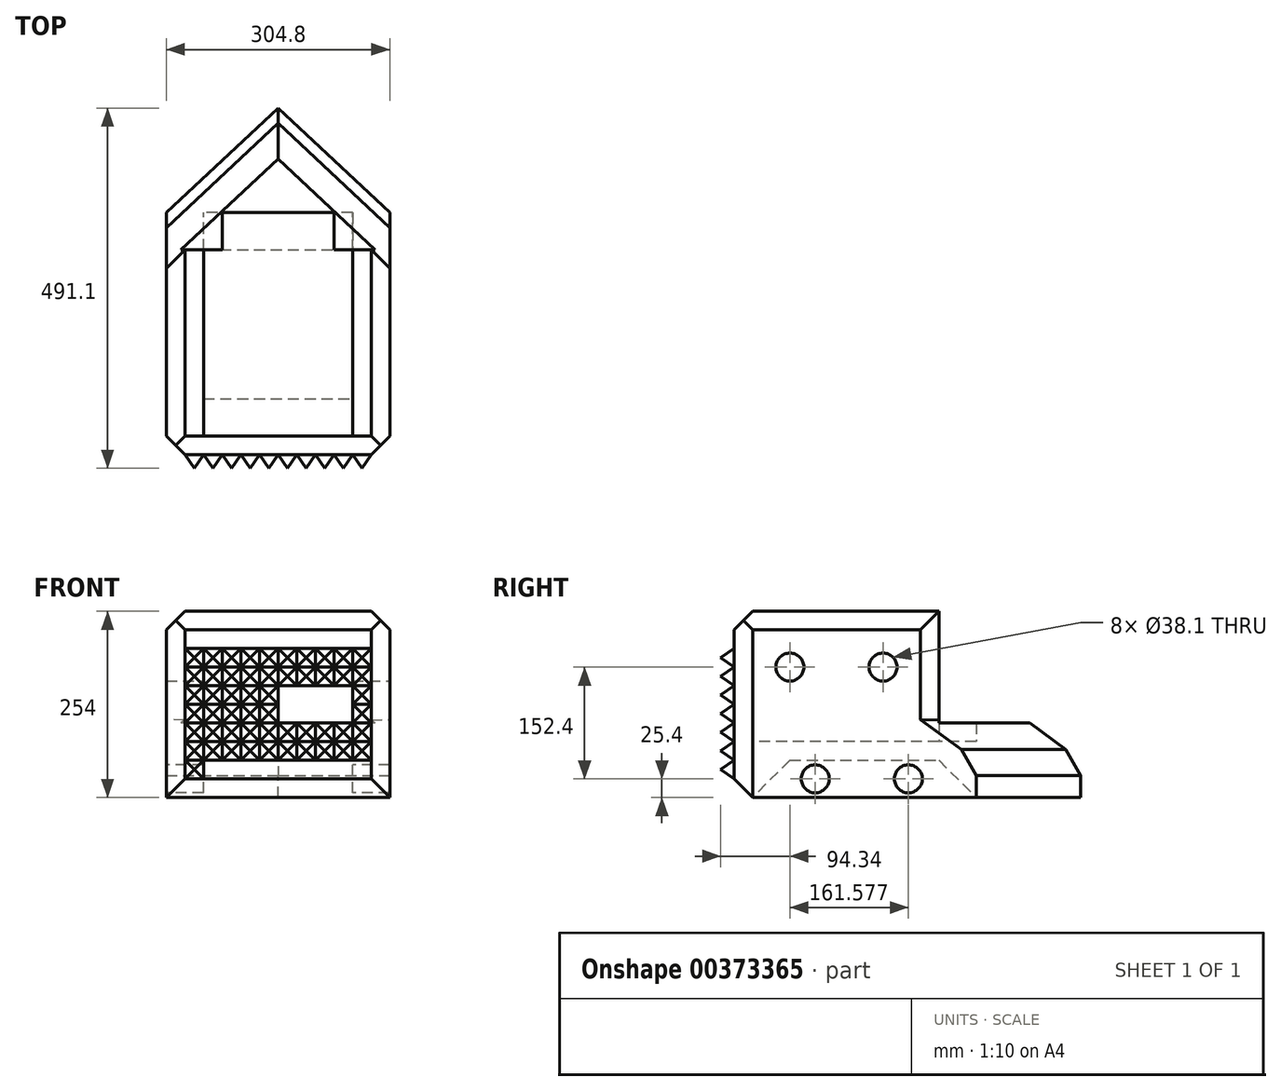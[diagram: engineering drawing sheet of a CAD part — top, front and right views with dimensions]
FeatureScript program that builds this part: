
annotation { "Feature Type Name" : "Feature", "Feature Type Description" : "" }
export const myFeature = defineFeature(function(context is Context, id is Id, definition is map)
    precondition{}
    {
        {
            var Q0;
            Q0=qCreatedBy(makeId("Top.planeOp"),FACE);
            var sketch = newSketch(context, id + "F0", { "sketchPlane" : qUnion([Q0])});
            skLineSegment(sketch, "E0.bottom", {"start": v(-152.4, 152.4) * mm, "end": v(152.4, 152.4) * mm});
            skLineSegment(sketch, "E0.top", {"start": v(-152.4, -152.4) * mm, "end": v(152.4, -152.4) * mm});
            skLineSegment(sketch, "E0.left", {"start": v(-152.4, 152.4) * mm, "end": v(-152.4, -152.4) * mm});
            skLineSegment(sketch, "E0.right", {"start": v(152.4, 152.4) * mm, "end": v(152.4, -152.4) * mm});
            skPoint(sketch, "E0.middle", {"position": v(0, 0) * mm});
            skSolve(sketch);
        }
        {
            var Q0;
            Q0 = qSketchRegion(id + "F0", true);
            extrude(context, id + "F1", {"entities" : qUnion([Q0]), "depth" : 25.4 * mm});
        }
        {
            var Q0;
            Q0=makeQuery(id+"F1.opExtrude","CAP_FACE",FACE,{"disambiguationData":[OSD([sQuery(id+"F0.wireOp",EDGE,"E0.bottom"),sQuery(id+"F0.wireOp",EDGE,"E0.top"),sQuery(id+"F0.wireOp",EDGE,"E0.left"),sQuery(id+"F0.wireOp",EDGE,"E0.right")])],"isStart":false});
            var sketch = newSketch(context, id + "F2", { "sketchPlane" : qUnion([Q0])});
            skLineSegment(sketch, "E1.bottom", {"start": v(-152.4, 152.4) * mm, "end": v(-101.6, 152.4) * mm});
            skLineSegment(sketch, "E1.top", {"start": v(-152.4, -152.4) * mm, "end": v(-101.6, -152.4) * mm});
            skLineSegment(sketch, "E1.left", {"start": v(-152.4, 152.4) * mm, "end": v(-152.4, -152.4) * mm});
            skLineSegment(sketch, "E1.right", {"start": v(-101.6, 152.4) * mm, "end": v(-101.6, -152.4) * mm});
            skLineSegment(sketch, "E2.bottom", {"start": v(152.4, -152.4) * mm, "end": v(101.6, -152.4) * mm});
            skLineSegment(sketch, "E2.top", {"start": v(152.4, 152.4) * mm, "end": v(101.6, 152.4) * mm});
            skLineSegment(sketch, "E2.left", {"start": v(152.4, -152.4) * mm, "end": v(152.4, 152.4) * mm});
            skLineSegment(sketch, "E2.right", {"start": v(101.6, -152.4) * mm, "end": v(101.6, 152.4) * mm});
            skLineSegment(sketch, "E3.bottom", {"start": v(-101.6, 152.4) * mm, "end": v(-76.2, 152.4) * mm});
            skLineSegment(sketch, "E3.top", {"start": v(-101.6, 101.6) * mm, "end": v(-76.2, 101.6) * mm});
            skLineSegment(sketch, "E3.left", {"start": v(-101.6, 152.4) * mm, "end": v(-101.6, 101.6) * mm});
            skLineSegment(sketch, "E3.right", {"start": v(-76.2, 152.4) * mm, "end": v(-76.2, 101.6) * mm});
            skLineSegment(sketch, "E4.bottom", {"start": v(101.6, 152.4) * mm, "end": v(76.2, 152.4) * mm});
            skLineSegment(sketch, "E4.top", {"start": v(101.6, 101.6) * mm, "end": v(76.2, 101.6) * mm});
            skLineSegment(sketch, "E4.left", {"start": v(101.6, 152.4) * mm, "end": v(101.6, 101.6) * mm});
            skLineSegment(sketch, "E4.right", {"start": v(76.2, 152.4) * mm, "end": v(76.2, 101.6) * mm});
            skSolve(sketch);
        }
        {
            var Q0;
            Q0=makeQuery(id+"F2.imprint","IMPRINT",FACE,{"disambiguationData":[TD([[makeQuery(id+"F2.imprint","IMPRINT",EDGE,{"derivedFrom":sQuery(id+"F2.wireOp",EDGE,"E2.bottom")}),1.0]])]});
            var Q1;
            Q1=makeQuery(id+"F2.imprint","IMPRINT",FACE,{"disambiguationData":[TD([[makeQuery(id+"F2.imprint","IMPRINT",EDGE,{"derivedFrom":sQuery(id+"F2.wireOp",EDGE,"E4.bottom")}),-1.0]])]});
            var Q2;
            Q2=makeQuery(id+"F2.imprint","IMPRINT",FACE,{"disambiguationData":[TD([[makeQuery(id+"F2.imprint","IMPRINT",EDGE,{"derivedFrom":sQuery(id+"F2.wireOp",EDGE,"E3.bottom")}),-1.0]])]});
            var Q3;
            Q3=makeQuery(id+"F2.imprint","IMPRINT",FACE,{"disambiguationData":[TD([[makeQuery(id+"F2.imprint","IMPRINT",EDGE,{"derivedFrom":sQuery(id+"F2.wireOp",EDGE,"E1.bottom")}),-1.0]])]});
            extrude(context, id + "F3", {"entities" : qUnion([Q0, Q1, Q2, Q3]), "operationType" : NewBodyOperationType.ADD, "depth" : 25.4 * mm});
        }
        {
            var Q0;
            Q0=makeQuery(id+"FkGgvWkWBMemayw_1.boolean.opBoolean","MERGE",FACE,{"derivedFrom":[makeQuery(id+"FRFY5aiqNvbobkp_1.boolean.opBoolean","MERGE",FACE,{"derivedFrom":[makeQuery(id+"F3.opExtrude","CAP_FACE",FACE,{"disambiguationData":[OSD([sQuery(id+"F2.wireOp",EDGE,"E1.bottom"),sQuery(id+"F2.wireOp",EDGE,"E1.top"),sQuery(id+"F2.wireOp",EDGE,"E1.left"),sQuery(id+"F2.wireOp",EDGE,"E1.right"),sQuery(id+"F2.wireOp",EDGE,"E2.bottom"),sQuery(id+"F2.wireOp",EDGE,"E2.top"),sQuery(id+"F2.wireOp",EDGE,"E2.left"),sQuery(id+"F2.wireOp",EDGE,"E2.right"),sQuery(id+"F2.wireOp",EDGE,"gtZrgzOz-b58x-KVUL-jsQg-DSi5dSDXwSVX.bottom"),sQuery(id+"F2.wireOp",EDGE,"gtZrgzOz-b58x-KVUL-jsQg-DSi5dSDXwSVX.top"),sQuery(id+"F2.wireOp",EDGE,"E3.bottom"),sQuery(id+"F2.wireOp",EDGE,"E3.top"),sQuery(id+"F2.wireOp",EDGE,"E3.right"),sQuery(id+"F2.wireOp",EDGE,"E4.bottom"),sQuery(id+"F2.wireOp",EDGE,"E4.top"),sQuery(id+"F2.wireOp",EDGE,"E4.right")])],"isStart":false}),makeQuery(id+"FRFY5aiqNvbobkp_1.opExtrude","CAP_FACE",FACE,{"disambiguationData":[OSD([sQuery(id+"FdvoQodGxraJRl4_1.wireOp",EDGE,"ubKTltfd-fttm-ud9w-CVmu-kFfNegf7EsK9"),sQuery(id+"FdvoQodGxraJRl4_1.wireOp",EDGE,"GuVsw8sI-SjNi-WbUd-Ecwz-Xx77keOuN9XW"),sQuery(id+"FdvoQodGxraJRl4_1.wireOp",EDGE,"aaOYgBz2-yths-JL3X-ABsj-uYR8tw8wiFr5")])],"isStart":true})]}),makeQuery(id+"FkGgvWkWBMemayw_1.opExtrude","CAP_FACE",FACE,{"disambiguationData":[OSD([sQuery(id+"FwGnvekFHA1S1A1_1.wireOp",EDGE,"zjP9bahP-IcYc-KR9K-D0dO-XseXDK0v0Trk"),sQuery(id+"FwGnvekFHA1S1A1_1.wireOp",EDGE,"3lqd1lpt-OsAJ-ImGJ-6Shh-clCQJiHXbUOp"),sQuery(id+"FwGnvekFHA1S1A1_1.wireOp",EDGE,"36x9WmHc-cpKm-z8fz-d8IO-fmrlZK17Axvm")])],"isStart":true})]});
            var sketch = newSketch(context, id + "F4", { "sketchPlane" : qUnion([Q0])});
            skLineSegment(sketch, "E5.bottom", {"start": v(-101.6, 101.6) * mm, "end": v(-152.4, 101.6) * mm});
            skLineSegment(sketch, "E5.top", {"start": v(-101.6, -152.4) * mm, "end": v(-152.4, -152.4) * mm});
            skLineSegment(sketch, "E5.left", {"start": v(-101.6, 101.6) * mm, "end": v(-101.6, -152.4) * mm});
            skLineSegment(sketch, "E5.right", {"start": v(-152.4, 101.6) * mm, "end": v(-152.4, -152.4) * mm});
            skLineSegment(sketch, "E6.bottom", {"start": v(152.4, -152.4) * mm, "end": v(101.6, -152.4) * mm});
            skLineSegment(sketch, "E6.top", {"start": v(152.4, 101.6) * mm, "end": v(101.6, 101.6) * mm});
            skLineSegment(sketch, "E6.left", {"start": v(152.4, -152.4) * mm, "end": v(152.4, 101.6) * mm});
            skLineSegment(sketch, "E6.right", {"start": v(101.6, -152.4) * mm, "end": v(101.6, 101.6) * mm});
            skSolve(sketch);
        }
        {
            var Q0;
            Q0 = qSketchRegion(id + "F4", true);
            extrude(context, id + "F5", {"entities" : qUnion([Q0]), "operationType" : NewBodyOperationType.ADD, "depth" : 152.4 * mm});
        }
        {
            var Q0;
            Q0=makeQuery(id+"F1.opExtrude","CAP_FACE",FACE,{"disambiguationData":[OSD([sQuery(id+"F0.wireOp",EDGE,"E0.bottom"),sQuery(id+"F0.wireOp",EDGE,"E0.top"),sQuery(id+"F0.wireOp",EDGE,"E0.left"),sQuery(id+"F0.wireOp",EDGE,"E0.right")])],"isStart":true});
            var sketch = newSketch(context, id + "F6", { "sketchPlane" : qUnion([Q0])});
            skLineSegment(sketch, "E7", {"start": v(152.4, -152.4) * mm, "end": v(0, -295.16) * mm});
            skLineSegment(sketch, "E8", {"start": v(0, -295.16) * mm, "end": v(-152.4, -152.4) * mm});
            skSolve(sketch);
        }
        {
            var Q0;
            Q0=makeQuery(id+"F6.imprint","IMPRINT",FACE,{"disambiguationData":[TD([[makeQuery(id+"F6.imprint","IMPRINT",EDGE,{"derivedFrom":sQuery(id+"F6.wireOp",EDGE,"E7")}),-1.0]])]});
            extrude(context, id + "F7", {"entities" : qUnion([Q0]), "operationType" : NewBodyOperationType.ADD, "oppositeDirection" : true, "depth" : 50.8 * mm});
        }
        {
            var Q0;
            Q0=makeQuery(id+"F7.opExtrude","CAP_EDGE",EDGE,{"disambiguationData":[OSD([sQuery(id+"F6.wireOp",EDGE,"E8")])],"isStart":false});
            var Q1;
            Q1=makeQuery(id+"F7.opExtrude","CAP_EDGE",EDGE,{"disambiguationData":[OSD([sQuery(id+"F6.wireOp",EDGE,"E7")])],"isStart":false});
            chamfer(context, id + "F8", {"entities" : qUnion([Q0, Q1]), "width" : 50.8 * mm, "tangentPropagation" : true});
        }
        {
            var Q0;
            Q0=makeQuery(id+"F5.boolean.opBoolean","MERGE",FACE,{"derivedFrom":[makeQuery(id+"F3.boolean.opBoolean","MERGE",FACE,{"derivedFrom":[makeQuery(id+"F1.opExtrude","SWEPT_FACE",FACE,{"disambiguationData":[OSD([sQuery(id+"F0.wireOp",EDGE,"E0.top")])]}),makeQuery(id+"F3.opExtrude","SWEPT_FACE",FACE,{"disambiguationData":[OSD([sQuery(id+"F2.wireOp",EDGE,"E1.top")])]}),makeQuery(id+"F3.opExtrude","SWEPT_FACE",FACE,{"disambiguationData":[OSD([sQuery(id+"F2.wireOp",EDGE,"E2.bottom")])]})]}),makeQuery(id+"F5.opExtrude","SWEPT_FACE",FACE,{"disambiguationData":[OSD([sQuery(id+"F4.wireOp",EDGE,"8l8OuRup-84i1-PPMk-ahTQ-howiFgtnHGYQ.top")])]}),makeQuery(id+"F5.opExtrude","SWEPT_FACE",FACE,{"disambiguationData":[OSD([sQuery(id+"F4.wireOp",EDGE,"KN1si1wC-PfOw-yzif-CKwp-hQymulGBh6hX.top")])]})]});
            var sketch = newSketch(context, id + "F9", { "sketchPlane" : qUnion([Q0])});
            skLineSegment(sketch, "E9.bottom", {"start": v(-152.4, 203.2) * mm, "end": v(152.4, 203.2) * mm});
            skLineSegment(sketch, "E9.top", {"start": v(-152.4, 0) * mm, "end": v(152.4, 0) * mm});
            skLineSegment(sketch, "E9.left", {"start": v(-152.4, 203.2) * mm, "end": v(-152.4, 0) * mm});
            skLineSegment(sketch, "E9.right", {"start": v(152.4, 203.2) * mm, "end": v(152.4, 0) * mm});
            skSolve(sketch);
        }
        {
            var Q0;
            Q0 = qSketchRegion(id + "F9", true);
            extrude(context, id + "F10", {"entities" : qUnion([Q0]), "operationType" : NewBodyOperationType.ADD, "depth" : 25.4 * mm});
        }
        {
            var Q0;
            Q0=makeQuery(id+"F10.opExtrude","CAP_FACE",FACE,{"disambiguationData":[OSD([sQuery(id+"F9.wireOp",EDGE,"E9.bottom"),sQuery(id+"F9.wireOp",EDGE,"E9.top"),sQuery(id+"F9.wireOp",EDGE,"E9.left"),sQuery(id+"F9.wireOp",EDGE,"E9.right")])],"isStart":false});
            var sketch = newSketch(context, id + "F11", { "sketchPlane" : qUnion([Q0])});
            skLineSegment(sketch, "E10", {"start": v(-152.4, 177.8) * mm, "end": v(152.4, 177.8) * mm});
            skLineSegment(sketch, "E11", {"start": v(-127, 177.8) * mm, "end": v(-127, 25.4) * mm});
            skLineSegment(sketch, "E12", {"start": v(127, 177.8) * mm, "end": v(127, 25.4) * mm});
            skLineSegment(sketch, "E13.bottom", {"start": v(-127, 177.8) * mm, "end": v(-101.6, 177.8) * mm});
            skLineSegment(sketch, "E13.top", {"start": v(-127, 152.4) * mm, "end": v(-101.6, 152.4) * mm});
            skLineSegment(sketch, "E13.left", {"start": v(-127, 177.8) * mm, "end": v(-127, 152.4) * mm});
            skLineSegment(sketch, "E13.right", {"start": v(-101.6, 177.8) * mm, "end": v(-101.6, 152.4) * mm});
            skLineSegment(sketch, "E14.bottom", {"start": v(-101.6, 152.4) * mm, "end": v(-76.2, 152.4) * mm});
            skLineSegment(sketch, "E14.top", {"start": v(-101.6, 177.8) * mm, "end": v(-76.2, 177.8) * mm});
            skLineSegment(sketch, "E14.left", {"start": v(-101.6, 152.4) * mm, "end": v(-101.6, 177.8) * mm});
            skLineSegment(sketch, "E14.right", {"start": v(-76.2, 152.4) * mm, "end": v(-76.2, 177.8) * mm});
            skLineSegment(sketch, "E15.bottom", {"start": v(-76.2, 152.4) * mm, "end": v(-50.8, 152.4) * mm});
            skLineSegment(sketch, "E15.top", {"start": v(-76.2, 177.8) * mm, "end": v(-50.8, 177.8) * mm});
            skLineSegment(sketch, "E15.right", {"start": v(-50.8, 152.4) * mm, "end": v(-50.8, 177.8) * mm});
            skLineSegment(sketch, "E16.bottom", {"start": v(-50.8, 152.4) * mm, "end": v(-25.4, 152.4) * mm});
            skLineSegment(sketch, "E16.top", {"start": v(-50.8, 177.8) * mm, "end": v(-25.4, 177.8) * mm});
            skLineSegment(sketch, "E16.right", {"start": v(-25.4, 152.4) * mm, "end": v(-25.4, 177.8) * mm});
            skLineSegment(sketch, "E17.bottom", {"start": v(-25.4, 152.4) * mm, "end": v(0, 152.4) * mm});
            skLineSegment(sketch, "E17.top", {"start": v(-25.4, 177.8) * mm, "end": v(0, 177.8) * mm});
            skLineSegment(sketch, "E17.right", {"start": v(0, 152.4) * mm, "end": v(0, 177.8) * mm});
            skLineSegment(sketch, "E18.bottom", {"start": v(0, 152.4) * mm, "end": v(25.4, 152.4) * mm});
            skLineSegment(sketch, "E18.top", {"start": v(0, 177.8) * mm, "end": v(25.4, 177.8) * mm});
            skLineSegment(sketch, "E18.right", {"start": v(25.4, 152.4) * mm, "end": v(25.4, 177.8) * mm});
            skLineSegment(sketch, "E19.bottom", {"start": v(25.4, 152.4) * mm, "end": v(50.8, 152.4) * mm});
            skLineSegment(sketch, "E19.top", {"start": v(25.4, 177.8) * mm, "end": v(50.8, 177.8) * mm});
            skLineSegment(sketch, "E19.right", {"start": v(50.8, 152.4) * mm, "end": v(50.8, 177.8) * mm});
            skLineSegment(sketch, "E20.bottom", {"start": v(50.8, 152.4) * mm, "end": v(76.2, 152.4) * mm});
            skLineSegment(sketch, "E20.top", {"start": v(50.8, 177.8) * mm, "end": v(76.2, 177.8) * mm});
            skLineSegment(sketch, "E20.right", {"start": v(76.2, 152.4) * mm, "end": v(76.2, 177.8) * mm});
            skLineSegment(sketch, "E21.bottom", {"start": v(76.2, 152.4) * mm, "end": v(101.6, 152.4) * mm});
            skLineSegment(sketch, "E21.top", {"start": v(76.2, 177.8) * mm, "end": v(101.6, 177.8) * mm});
            skLineSegment(sketch, "E21.right", {"start": v(101.6, 152.4) * mm, "end": v(101.6, 177.8) * mm});
            skLineSegment(sketch, "E22.bottom", {"start": v(101.6, 152.4) * mm, "end": v(127, 152.4) * mm});
            skLineSegment(sketch, "E22.top", {"start": v(101.6, 177.8) * mm, "end": v(127, 177.8) * mm});
            skLineSegment(sketch, "E22.right", {"start": v(127, 152.4) * mm, "end": v(127, 177.8) * mm});
            skLineSegment(sketch, "E23.top", {"start": v(-127, 127) * mm, "end": v(-101.6, 127) * mm});
            skLineSegment(sketch, "E23.left", {"start": v(-127, 152.4) * mm, "end": v(-127, 127) * mm});
            skLineSegment(sketch, "E23.right", {"start": v(-101.6, 152.4) * mm, "end": v(-101.6, 127) * mm});
            skLineSegment(sketch, "E24.bottom", {"start": v(-101.6, 127) * mm, "end": v(-76.2, 127) * mm});
            skLineSegment(sketch, "E24.left", {"start": v(-101.6, 127) * mm, "end": v(-101.6, 152.4) * mm});
            skLineSegment(sketch, "E24.right", {"start": v(-76.2, 127) * mm, "end": v(-76.2, 152.4) * mm});
            skLineSegment(sketch, "E25.bottom", {"start": v(-76.2, 127) * mm, "end": v(-50.8, 127) * mm});
            skLineSegment(sketch, "E25.right", {"start": v(-50.8, 127) * mm, "end": v(-50.8, 152.4) * mm});
            skLineSegment(sketch, "E26.bottom", {"start": v(-50.8, 127) * mm, "end": v(-25.4, 127) * mm});
            skLineSegment(sketch, "E26.right", {"start": v(-25.4, 127) * mm, "end": v(-25.4, 152.4) * mm});
            skLineSegment(sketch, "E27.bottom", {"start": v(-25.4, 127) * mm, "end": v(0, 127) * mm});
            skLineSegment(sketch, "E27.right", {"start": v(0, 127) * mm, "end": v(0, 152.4) * mm});
            skLineSegment(sketch, "E28.bottom", {"start": v(0, 127) * mm, "end": v(25.4, 127) * mm});
            skLineSegment(sketch, "E28.right", {"start": v(25.4, 127) * mm, "end": v(25.4, 152.4) * mm});
            skLineSegment(sketch, "E29.bottom", {"start": v(25.4, 127) * mm, "end": v(50.8, 127) * mm});
            skLineSegment(sketch, "E29.right", {"start": v(50.8, 127) * mm, "end": v(50.8, 152.4) * mm});
            skLineSegment(sketch, "E30.bottom", {"start": v(50.8, 127) * mm, "end": v(76.2, 127) * mm});
            skLineSegment(sketch, "E30.right", {"start": v(76.2, 127) * mm, "end": v(76.2, 152.4) * mm});
            skLineSegment(sketch, "E31.bottom", {"start": v(76.2, 127) * mm, "end": v(101.6, 127) * mm});
            skLineSegment(sketch, "E31.right", {"start": v(101.6, 127) * mm, "end": v(101.6, 152.4) * mm});
            skLineSegment(sketch, "E32.bottom", {"start": v(101.6, 127) * mm, "end": v(127, 127) * mm});
            skLineSegment(sketch, "E32.right", {"start": v(127, 127) * mm, "end": v(127, 152.4) * mm});
            skLineSegment(sketch, "E33.top", {"start": v(-127, 101.6) * mm, "end": v(-101.6, 101.6) * mm});
            skLineSegment(sketch, "E33.left", {"start": v(-127, 127) * mm, "end": v(-127, 101.6) * mm});
            skLineSegment(sketch, "E33.right", {"start": v(-101.6, 127) * mm, "end": v(-101.6, 101.6) * mm});
            skLineSegment(sketch, "E34.bottom", {"start": v(-101.6, 101.6) * mm, "end": v(-76.2, 101.6) * mm});
            skLineSegment(sketch, "E34.left", {"start": v(-101.6, 101.6) * mm, "end": v(-101.6, 127) * mm});
            skLineSegment(sketch, "E34.right", {"start": v(-76.2, 101.6) * mm, "end": v(-76.2, 127) * mm});
            skLineSegment(sketch, "E35.bottom", {"start": v(-76.2, 101.6) * mm, "end": v(-50.8, 101.6) * mm});
            skLineSegment(sketch, "E35.right", {"start": v(-50.8, 101.6) * mm, "end": v(-50.8, 127) * mm});
            skLineSegment(sketch, "E36.bottom", {"start": v(-50.8, 101.6) * mm, "end": v(-25.4, 101.6) * mm});
            skLineSegment(sketch, "E36.right", {"start": v(-25.4, 101.6) * mm, "end": v(-25.4, 127) * mm});
            skLineSegment(sketch, "E37.bottom", {"start": v(-25.4, 101.6) * mm, "end": v(0, 101.6) * mm});
            skLineSegment(sketch, "E37.right", {"start": v(0, 101.6) * mm, "end": v(0, 127) * mm});
            skLineSegment(sketch, "E38.bottom", {"start": v(0, 101.6) * mm, "end": v(25.4, 101.6) * mm});
            skLineSegment(sketch, "E38.right", {"start": v(25.4, 101.6) * mm, "end": v(25.4, 127) * mm});
            skLineSegment(sketch, "E39.bottom", {"start": v(25.4, 101.6) * mm, "end": v(50.8, 101.6) * mm});
            skLineSegment(sketch, "E39.right", {"start": v(50.8, 101.6) * mm, "end": v(50.8, 127) * mm});
            skLineSegment(sketch, "E40.bottom", {"start": v(50.8, 101.6) * mm, "end": v(76.2, 101.6) * mm});
            skLineSegment(sketch, "E40.right", {"start": v(76.2, 101.6) * mm, "end": v(76.2, 127) * mm});
            skLineSegment(sketch, "E41.bottom", {"start": v(76.2, 101.6) * mm, "end": v(101.6, 101.6) * mm});
            skLineSegment(sketch, "E41.right", {"start": v(101.6, 101.6) * mm, "end": v(101.6, 127) * mm});
            skLineSegment(sketch, "E42.bottom", {"start": v(101.6, 101.6) * mm, "end": v(127, 101.6) * mm});
            skLineSegment(sketch, "E42.right", {"start": v(127, 101.6) * mm, "end": v(127, 127) * mm});
            skLineSegment(sketch, "E43.top", {"start": v(101.6, 76.2) * mm, "end": v(127, 76.2) * mm});
            skLineSegment(sketch, "E43.left", {"start": v(101.6, 101.6) * mm, "end": v(101.6, 76.2) * mm});
            skLineSegment(sketch, "E43.right", {"start": v(127, 101.6) * mm, "end": v(127, 76.2) * mm});
            skLineSegment(sketch, "E44.bottom", {"start": v(101.6, 76.2) * mm, "end": v(76.2, 76.2) * mm});
            skLineSegment(sketch, "E44.top", {"start": v(101.6, 101.6) * mm, "end": v(76.2, 101.6) * mm});
            skLineSegment(sketch, "E44.left", {"start": v(101.6, 76.2) * mm, "end": v(101.6, 101.6) * mm});
            skLineSegment(sketch, "E44.right", {"start": v(76.2, 76.2) * mm, "end": v(76.2, 101.6) * mm});
            skLineSegment(sketch, "E45.bottom", {"start": v(76.2, 76.2) * mm, "end": v(50.8, 76.2) * mm});
            skLineSegment(sketch, "E45.top", {"start": v(76.2, 101.6) * mm, "end": v(50.8, 101.6) * mm});
            skLineSegment(sketch, "E45.right", {"start": v(50.8, 76.2) * mm, "end": v(50.8, 101.6) * mm});
            skLineSegment(sketch, "E46.bottom", {"start": v(50.8, 76.2) * mm, "end": v(25.4, 76.2) * mm});
            skLineSegment(sketch, "E46.top", {"start": v(50.8, 101.6) * mm, "end": v(25.4, 101.6) * mm});
            skLineSegment(sketch, "E46.right", {"start": v(25.4, 76.2) * mm, "end": v(25.4, 101.6) * mm});
            skLineSegment(sketch, "E47.bottom", {"start": v(25.4, 76.2) * mm, "end": v(0, 76.2) * mm});
            skLineSegment(sketch, "E47.top", {"start": v(25.4, 101.6) * mm, "end": v(0, 101.6) * mm});
            skLineSegment(sketch, "E47.right", {"start": v(0, 76.2) * mm, "end": v(0, 101.6) * mm});
            skLineSegment(sketch, "E48.top", {"start": v(-25.4, 76.2) * mm, "end": v(0, 76.2) * mm});
            skLineSegment(sketch, "E48.left", {"start": v(-25.4, 101.6) * mm, "end": v(-25.4, 76.2) * mm});
            skLineSegment(sketch, "E48.right", {"start": v(0, 101.6) * mm, "end": v(0, 76.2) * mm});
            skLineSegment(sketch, "E49.top", {"start": v(-50.8, 76.2) * mm, "end": v(-25.4, 76.2) * mm});
            skLineSegment(sketch, "E49.left", {"start": v(-50.8, 101.6) * mm, "end": v(-50.8, 76.2) * mm});
            skLineSegment(sketch, "E50.top", {"start": v(-76.2, 76.2) * mm, "end": v(-50.8, 76.2) * mm});
            skLineSegment(sketch, "E50.left", {"start": v(-76.2, 101.6) * mm, "end": v(-76.2, 76.2) * mm});
            skLineSegment(sketch, "E51.top", {"start": v(-101.6, 76.2) * mm, "end": v(-76.2, 76.2) * mm});
            skLineSegment(sketch, "E51.left", {"start": v(-101.6, 101.6) * mm, "end": v(-101.6, 76.2) * mm});
            skLineSegment(sketch, "E52.top", {"start": v(-127, 76.2) * mm, "end": v(-101.6, 76.2) * mm});
            skLineSegment(sketch, "E52.left", {"start": v(-127, 101.6) * mm, "end": v(-127, 76.2) * mm});
            skLineSegment(sketch, "E53.top", {"start": v(-127, 50.8) * mm, "end": v(-101.6, 50.8) * mm});
            skLineSegment(sketch, "E53.left", {"start": v(-127, 76.2) * mm, "end": v(-127, 50.8) * mm});
            skLineSegment(sketch, "E53.right", {"start": v(-101.6, 76.2) * mm, "end": v(-101.6, 50.8) * mm});
            skLineSegment(sketch, "E54.bottom", {"start": v(-101.6, 50.8) * mm, "end": v(-76.2, 50.8) * mm});
            skLineSegment(sketch, "E54.left", {"start": v(-101.6, 50.8) * mm, "end": v(-101.6, 76.2) * mm});
            skLineSegment(sketch, "E54.right", {"start": v(-76.2, 50.8) * mm, "end": v(-76.2, 76.2) * mm});
            skLineSegment(sketch, "E55.bottom", {"start": v(-76.2, 50.8) * mm, "end": v(-50.8, 50.8) * mm});
            skLineSegment(sketch, "E55.right", {"start": v(-50.8, 50.8) * mm, "end": v(-50.8, 76.2) * mm});
            skLineSegment(sketch, "E56.bottom", {"start": v(-50.8, 50.8) * mm, "end": v(-25.4, 50.8) * mm});
            skLineSegment(sketch, "E56.right", {"start": v(-25.4, 50.8) * mm, "end": v(-25.4, 76.2) * mm});
            skLineSegment(sketch, "E57.bottom", {"start": v(-25.4, 50.8) * mm, "end": v(0, 50.8) * mm});
            skLineSegment(sketch, "E57.right", {"start": v(0, 50.8) * mm, "end": v(0, 76.2) * mm});
            skLineSegment(sketch, "E58.bottom", {"start": v(0, 50.8) * mm, "end": v(25.4, 50.8) * mm});
            skLineSegment(sketch, "E58.top", {"start": v(0, 76.2) * mm, "end": v(25.4, 76.2) * mm});
            skLineSegment(sketch, "E58.right", {"start": v(25.4, 50.8) * mm, "end": v(25.4, 76.2) * mm});
            skLineSegment(sketch, "E59.bottom", {"start": v(25.4, 50.8) * mm, "end": v(50.8, 50.8) * mm});
            skLineSegment(sketch, "E59.top", {"start": v(25.4, 76.2) * mm, "end": v(50.8, 76.2) * mm});
            skLineSegment(sketch, "E59.right", {"start": v(50.8, 50.8) * mm, "end": v(50.8, 76.2) * mm});
            skLineSegment(sketch, "E60.bottom", {"start": v(50.8, 50.8) * mm, "end": v(76.2, 50.8) * mm});
            skLineSegment(sketch, "E60.top", {"start": v(50.8, 76.2) * mm, "end": v(76.2, 76.2) * mm});
            skLineSegment(sketch, "E60.right", {"start": v(76.2, 50.8) * mm, "end": v(76.2, 76.2) * mm});
            skLineSegment(sketch, "E61.bottom", {"start": v(76.2, 50.8) * mm, "end": v(101.6, 50.8) * mm});
            skLineSegment(sketch, "E61.top", {"start": v(76.2, 76.2) * mm, "end": v(101.6, 76.2) * mm});
            skLineSegment(sketch, "E61.right", {"start": v(101.6, 50.8) * mm, "end": v(101.6, 76.2) * mm});
            skLineSegment(sketch, "E62.bottom", {"start": v(101.6, 50.8) * mm, "end": v(127, 50.8) * mm});
            skLineSegment(sketch, "E62.right", {"start": v(127, 50.8) * mm, "end": v(127, 76.2) * mm});
            skLineSegment(sketch, "E63.top", {"start": v(-127, 25.4) * mm, "end": v(-101.6, 25.4) * mm});
            skLineSegment(sketch, "E63.left", {"start": v(-127, 50.8) * mm, "end": v(-127, 25.4) * mm});
            skLineSegment(sketch, "E63.right", {"start": v(-101.6, 50.8) * mm, "end": v(-101.6, 25.4) * mm});
            skLineSegment(sketch, "E64.top", {"start": v(-101.6, 25.4) * mm, "end": v(-76.2, 25.4) * mm});
            skLineSegment(sketch, "E64.right", {"start": v(-76.2, 50.8) * mm, "end": v(-76.2, 25.4) * mm});
            skLineSegment(sketch, "E65.bottom", {"start": v(-76.2, 25.4) * mm, "end": v(-50.8, 25.4) * mm});
            skLineSegment(sketch, "E65.left", {"start": v(-76.2, 25.4) * mm, "end": v(-76.2, 50.8) * mm});
            skLineSegment(sketch, "E65.right", {"start": v(-50.8, 25.4) * mm, "end": v(-50.8, 50.8) * mm});
            skLineSegment(sketch, "E66.bottom", {"start": v(-50.8, 25.4) * mm, "end": v(-25.4, 25.4) * mm});
            skLineSegment(sketch, "E66.right", {"start": v(-25.4, 25.4) * mm, "end": v(-25.4, 50.8) * mm});
            skLineSegment(sketch, "E67.bottom", {"start": v(-25.4, 25.4) * mm, "end": v(0, 25.4) * mm});
            skLineSegment(sketch, "E67.right", {"start": v(0, 25.4) * mm, "end": v(0, 50.8) * mm});
            skLineSegment(sketch, "E68.bottom", {"start": v(0, 25.4) * mm, "end": v(25.4, 25.4) * mm});
            skLineSegment(sketch, "E68.right", {"start": v(25.4, 25.4) * mm, "end": v(25.4, 50.8) * mm});
            skLineSegment(sketch, "E69.bottom", {"start": v(25.4, 25.4) * mm, "end": v(50.8, 25.4) * mm});
            skLineSegment(sketch, "E69.right", {"start": v(50.8, 25.4) * mm, "end": v(50.8, 50.8) * mm});
            skLineSegment(sketch, "E70.bottom", {"start": v(50.8, 25.4) * mm, "end": v(76.2, 25.4) * mm});
            skLineSegment(sketch, "E70.right", {"start": v(76.2, 25.4) * mm, "end": v(76.2, 50.8) * mm});
            skLineSegment(sketch, "E71.bottom", {"start": v(76.2, 25.4) * mm, "end": v(101.6, 25.4) * mm});
            skLineSegment(sketch, "E71.right", {"start": v(101.6, 25.4) * mm, "end": v(101.6, 50.8) * mm});
            skLineSegment(sketch, "E72.bottom", {"start": v(101.6, 25.4) * mm, "end": v(127, 25.4) * mm});
            skLineSegment(sketch, "E72.right", {"start": v(127, 25.4) * mm, "end": v(127, 50.8) * mm});
            skSolve(sketch);
        }
        {
            var Q0;
            Q0=makeQuery(id+"F11.imprint","IMPRINT",FACE,{"disambiguationData":[TD([[makeQuery(id+"F11.imprint","IMPRINT",EDGE,{"derivedFrom":sQuery(id+"F11.wireOp",EDGE,"E13.bottom")}),-1.0]])]});
            var Q1;
            Q1=makeQuery(id+"F11.imprint","IMPRINT",FACE,{"disambiguationData":[TD([[makeQuery(id+"F11.imprint","IMPRINT",EDGE,{"derivedFrom":sQuery(id+"F11.wireOp",EDGE,"E14.bottom")}),-1.0]])]});
            var Q2;
            Q2=makeQuery(id+"F11.imprint","IMPRINT",FACE,{"disambiguationData":[TD([[makeQuery(id+"F11.imprint","IMPRINT",EDGE,{"derivedFrom":sQuery(id+"F11.wireOp",EDGE,"E15.top")}),-1.0]])]});
            var Q3;
            Q3=makeQuery(id+"F11.imprint","IMPRINT",FACE,{"disambiguationData":[TD([[makeQuery(id+"F11.imprint","IMPRINT",EDGE,{"derivedFrom":sQuery(id+"F11.wireOp",EDGE,"E16.bottom")}),-1.0]])]});
            var Q4;
            Q4=makeQuery(id+"F11.imprint","IMPRINT",FACE,{"disambiguationData":[TD([[makeQuery(id+"F11.imprint","IMPRINT",EDGE,{"derivedFrom":sQuery(id+"F11.wireOp",EDGE,"E17.top")}),-1.0]])]});
            var Q5;
            Q5=makeQuery(id+"F11.imprint","IMPRINT",FACE,{"disambiguationData":[TD([[makeQuery(id+"F11.imprint","IMPRINT",EDGE,{"derivedFrom":sQuery(id+"F11.wireOp",EDGE,"E18.bottom")}),-1.0]])]});
            var Q6;
            Q6=makeQuery(id+"F11.imprint","IMPRINT",FACE,{"disambiguationData":[TD([[makeQuery(id+"F11.imprint","IMPRINT",EDGE,{"derivedFrom":sQuery(id+"F11.wireOp",EDGE,"E19.top")}),-1.0]])]});
            var Q7;
            Q7=makeQuery(id+"F11.imprint","IMPRINT",FACE,{"disambiguationData":[TD([[makeQuery(id+"F11.imprint","IMPRINT",EDGE,{"derivedFrom":sQuery(id+"F11.wireOp",EDGE,"E20.bottom")}),-1.0]])]});
            var Q8;
            Q8=makeQuery(id+"F11.imprint","IMPRINT",FACE,{"disambiguationData":[TD([[makeQuery(id+"F11.imprint","IMPRINT",EDGE,{"derivedFrom":sQuery(id+"F11.wireOp",EDGE,"E21.top")}),-1.0]])]});
            var Q9;
            Q9=makeQuery(id+"F11.imprint","IMPRINT",FACE,{"disambiguationData":[TD([[makeQuery(id+"F11.imprint","IMPRINT",EDGE,{"derivedFrom":sQuery(id+"F11.wireOp",EDGE,"E22.bottom")}),-1.0]])]});
            var Q10;
            Q10=makeQuery(id+"F11.imprint","IMPRINT",FACE,{"disambiguationData":[TD([[makeQuery(id+"F11.imprint","IMPRINT",EDGE,{"derivedFrom":sQuery(id+"F11.wireOp",EDGE,"E31.bottom")}),-1.0]])]});
            var Q11;
            Q11=makeQuery(id+"F11.imprint","IMPRINT",FACE,{"disambiguationData":[TD([[makeQuery(id+"F11.imprint","IMPRINT",EDGE,{"derivedFrom":sQuery(id+"F11.wireOp",EDGE,"E42.bottom")}),-1.0]])]});
            var Q12;
            Q12=makeQuery(id+"F11.imprint","IMPRINT",FACE,{"disambiguationData":[TD([[makeQuery(id+"F11.imprint","IMPRINT",EDGE,{"derivedFrom":sQuery(id+"F11.wireOp",EDGE,"E61.top")}),-1.0]])]});
            var Q13;
            Q13=makeQuery(id+"F11.imprint","IMPRINT",FACE,{"disambiguationData":[TD([[makeQuery(id+"F11.imprint","IMPRINT",EDGE,{"derivedFrom":sQuery(id+"F11.wireOp",EDGE,"E72.bottom")}),1.0]])]});
            var Q14;
            Q14=makeQuery(id+"F11.imprint","IMPRINT",FACE,{"disambiguationData":[TD([[makeQuery(id+"F11.imprint","IMPRINT",EDGE,{"derivedFrom":sQuery(id+"F11.wireOp",EDGE,"E70.bottom")}),1.0]])]});
            var Q15;
            Q15=makeQuery(id+"F11.imprint","IMPRINT",FACE,{"disambiguationData":[TD([[makeQuery(id+"F11.imprint","IMPRINT",EDGE,{"derivedFrom":sQuery(id+"F11.wireOp",EDGE,"E45.top")}),1.0]])]});
            var Q16;
            Q16=makeQuery(id+"F11.imprint","IMPRINT",FACE,{"disambiguationData":[TD([[makeQuery(id+"F11.imprint","IMPRINT",EDGE,{"derivedFrom":sQuery(id+"F11.wireOp",EDGE,"E29.bottom")}),-1.0]])]});
            var Q17;
            Q17=makeQuery(id+"F11.imprint","IMPRINT",FACE,{"disambiguationData":[TD([[makeQuery(id+"F11.imprint","IMPRINT",EDGE,{"derivedFrom":sQuery(id+"F11.wireOp",EDGE,"E59.top")}),-1.0]])]});
            var Q18;
            Q18=makeQuery(id+"F11.imprint","IMPRINT",FACE,{"disambiguationData":[TD([[makeQuery(id+"F11.imprint","IMPRINT",EDGE,{"derivedFrom":sQuery(id+"F11.wireOp",EDGE,"E68.bottom")}),1.0]])]});
            var Q19;
            Q19=makeQuery(id+"F11.imprint","IMPRINT",FACE,{"disambiguationData":[TD([[makeQuery(id+"F11.imprint","IMPRINT",EDGE,{"derivedFrom":sQuery(id+"F11.wireOp",EDGE,"E47.top")}),1.0]])]});
            var Q20;
            Q20=makeQuery(id+"F11.imprint","IMPRINT",FACE,{"disambiguationData":[TD([[makeQuery(id+"F11.imprint","IMPRINT",EDGE,{"derivedFrom":sQuery(id+"F11.wireOp",EDGE,"E27.bottom")}),-1.0]])]});
            var Q21;
            Q21=makeQuery(id+"F11.imprint","IMPRINT",FACE,{"disambiguationData":[TD([[makeQuery(id+"F11.imprint","IMPRINT",EDGE,{"derivedFrom":sQuery(id+"F11.wireOp",EDGE,"E48.top")}),-1.0]])]});
            var Q22;
            Q22=makeQuery(id+"F11.imprint","IMPRINT",FACE,{"disambiguationData":[TD([[makeQuery(id+"F11.imprint","IMPRINT",EDGE,{"derivedFrom":sQuery(id+"F11.wireOp",EDGE,"E66.bottom")}),1.0]])]});
            var Q23;
            Q23=makeQuery(id+"F11.imprint","IMPRINT",FACE,{"disambiguationData":[TD([[makeQuery(id+"F11.imprint","IMPRINT",EDGE,{"derivedFrom":sQuery(id+"F11.wireOp",EDGE,"E36.bottom")}),-1.0]])]});
            var Q24;
            Q24=makeQuery(id+"F11.imprint","IMPRINT",FACE,{"disambiguationData":[TD([[makeQuery(id+"F11.imprint","IMPRINT",EDGE,{"derivedFrom":sQuery(id+"F11.wireOp",EDGE,"E25.bottom")}),-1.0]])]});
            var Q25;
            Q25=makeQuery(id+"F11.imprint","IMPRINT",FACE,{"disambiguationData":[TD([[makeQuery(id+"F11.imprint","IMPRINT",EDGE,{"derivedFrom":sQuery(id+"F11.wireOp",EDGE,"E50.top")}),-1.0]])]});
            var Q26;
            Q26=makeQuery(id+"F11.imprint","IMPRINT",FACE,{"disambiguationData":[TD([[makeQuery(id+"F11.imprint","IMPRINT",EDGE,{"derivedFrom":sQuery(id+"F11.wireOp",EDGE,"E54.bottom")}),-1.0]])]});
            var Q27;
            Q27=makeQuery(id+"F11.imprint","IMPRINT",FACE,{"disambiguationData":[TD([[makeQuery(id+"F11.imprint","IMPRINT",EDGE,{"derivedFrom":sQuery(id+"F11.wireOp",EDGE,"E34.bottom")}),-1.0]])]});
            var Q28;
            Q28=makeQuery(id+"F11.imprint","IMPRINT",FACE,{"disambiguationData":[TD([[makeQuery(id+"F11.imprint","IMPRINT",EDGE,{"derivedFrom":sQuery(id+"F11.wireOp",EDGE,"E23.top")}),-1.0]])]});
            var Q29;
            Q29=makeQuery(id+"F11.imprint","IMPRINT",FACE,{"disambiguationData":[TD([[makeQuery(id+"F11.imprint","IMPRINT",EDGE,{"derivedFrom":sQuery(id+"F11.wireOp",EDGE,"E52.top")}),-1.0]])]});
            extrude(context, id + "F12", {"entities" : qUnion([Q0, Q1, Q2, Q3, Q4, Q5, Q6, Q7, Q8, Q9, Q10, Q11, Q12, Q13, Q14, Q15, Q16, Q17, Q18, Q19, Q20, Q21, Q22, Q23, Q24, Q25, Q26, Q27, Q28, Q29]), "operationType" : NewBodyOperationType.ADD, "depth" : 25.4 * mm, "hasDraft" : true, "draftAngle" : 35 * degree, "draftPullDirection" : true});
        }
        {
            var Q0;
            Q0=makeQuery(id+"F11.imprint","IMPRINT",FACE,{"disambiguationData":[TD([[makeQuery(id+"F11.imprint","IMPRINT",EDGE,{"derivedFrom":sQuery(id+"F11.wireOp",EDGE,"E14.top")}),-1.0]])]});
            var Q1;
            Q1=makeQuery(id+"F11.imprint","IMPRINT",FACE,{"disambiguationData":[TD([[makeQuery(id+"F11.imprint","IMPRINT",EDGE,{"derivedFrom":sQuery(id+"F11.wireOp",EDGE,"E15.bottom")}),-1.0]])]});
            var Q2;
            Q2=makeQuery(id+"F11.imprint","IMPRINT",FACE,{"disambiguationData":[TD([[makeQuery(id+"F11.imprint","IMPRINT",EDGE,{"derivedFrom":sQuery(id+"F11.wireOp",EDGE,"E16.top")}),-1.0]])]});
            var Q3;
            Q3=makeQuery(id+"F11.imprint","IMPRINT",FACE,{"disambiguationData":[TD([[makeQuery(id+"F11.imprint","IMPRINT",EDGE,{"derivedFrom":sQuery(id+"F11.wireOp",EDGE,"E17.bottom")}),-1.0]])]});
            var Q4;
            Q4=makeQuery(id+"F11.imprint","IMPRINT",FACE,{"disambiguationData":[TD([[makeQuery(id+"F11.imprint","IMPRINT",EDGE,{"derivedFrom":sQuery(id+"F11.wireOp",EDGE,"E13.top")}),-1.0]])]});
            var Q5;
            Q5=makeQuery(id+"F11.imprint","IMPRINT",FACE,{"disambiguationData":[TD([[makeQuery(id+"F11.imprint","IMPRINT",EDGE,{"derivedFrom":sQuery(id+"F11.wireOp",EDGE,"E24.bottom")}),-1.0]])]});
            var Q6;
            Q6=makeQuery(id+"F11.imprint","IMPRINT",FACE,{"disambiguationData":[TD([[makeQuery(id+"F11.imprint","IMPRINT",EDGE,{"derivedFrom":sQuery(id+"F11.wireOp",EDGE,"E33.top")}),-1.0]])]});
            var Q7;
            Q7=makeQuery(id+"F11.imprint","IMPRINT",FACE,{"disambiguationData":[TD([[makeQuery(id+"F11.imprint","IMPRINT",EDGE,{"derivedFrom":sQuery(id+"F11.wireOp",EDGE,"E51.top")}),-1.0]])]});
            var Q8;
            Q8=makeQuery(id+"F11.imprint","IMPRINT",FACE,{"disambiguationData":[TD([[makeQuery(id+"F11.imprint","IMPRINT",EDGE,{"derivedFrom":sQuery(id+"F11.wireOp",EDGE,"E53.top")}),-1.0]])]});
            var Q9;
            Q9=makeQuery(id+"F11.imprint","IMPRINT",FACE,{"disambiguationData":[TD([[makeQuery(id+"F11.imprint","IMPRINT",EDGE,{"derivedFrom":sQuery(id+"F11.wireOp",EDGE,"E65.bottom")}),1.0]])]});
            var Q10;
            Q10=makeQuery(id+"F11.imprint","IMPRINT",FACE,{"disambiguationData":[TD([[makeQuery(id+"F11.imprint","IMPRINT",EDGE,{"derivedFrom":sQuery(id+"F11.wireOp",EDGE,"E35.bottom")}),-1.0]])]});
            var Q11;
            Q11=makeQuery(id+"F11.imprint","IMPRINT",FACE,{"disambiguationData":[TD([[makeQuery(id+"F11.imprint","IMPRINT",EDGE,{"derivedFrom":sQuery(id+"F11.wireOp",EDGE,"E26.bottom")}),-1.0]])]});
            var Q12;
            Q12=makeQuery(id+"F11.imprint","IMPRINT",FACE,{"disambiguationData":[TD([[makeQuery(id+"F11.imprint","IMPRINT",EDGE,{"derivedFrom":sQuery(id+"F11.wireOp",EDGE,"E37.bottom")}),-1.0]])]});
            var Q13;
            Q13=makeQuery(id+"F11.imprint","IMPRINT",FACE,{"disambiguationData":[TD([[makeQuery(id+"F11.imprint","IMPRINT",EDGE,{"derivedFrom":sQuery(id+"F11.wireOp",EDGE,"E49.top")}),-1.0]])]});
            var Q14;
            Q14=makeQuery(id+"F11.imprint","IMPRINT",FACE,{"disambiguationData":[TD([[makeQuery(id+"F11.imprint","IMPRINT",EDGE,{"derivedFrom":sQuery(id+"F11.wireOp",EDGE,"E67.bottom")}),1.0]])]});
            var Q15;
            Q15=makeQuery(id+"F11.imprint","IMPRINT",FACE,{"disambiguationData":[TD([[makeQuery(id+"F11.imprint","IMPRINT",EDGE,{"derivedFrom":sQuery(id+"F11.wireOp",EDGE,"E18.top")}),-1.0]])]});
            var Q16;
            Q16=makeQuery(id+"F11.imprint","IMPRINT",FACE,{"disambiguationData":[TD([[makeQuery(id+"F11.imprint","IMPRINT",EDGE,{"derivedFrom":sQuery(id+"F11.wireOp",EDGE,"E28.bottom")}),-1.0]])]});
            var Q17;
            Q17=makeQuery(id+"F11.imprint","IMPRINT",FACE,{"disambiguationData":[TD([[makeQuery(id+"F11.imprint","IMPRINT",EDGE,{"derivedFrom":sQuery(id+"F11.wireOp",EDGE,"E58.top")}),-1.0]])]});
            var Q18;
            Q18=makeQuery(id+"F11.imprint","IMPRINT",FACE,{"disambiguationData":[TD([[makeQuery(id+"F11.imprint","IMPRINT",EDGE,{"derivedFrom":sQuery(id+"F11.wireOp",EDGE,"E46.top")}),1.0]])]});
            var Q19;
            Q19=makeQuery(id+"F11.imprint","IMPRINT",FACE,{"disambiguationData":[TD([[makeQuery(id+"F11.imprint","IMPRINT",EDGE,{"derivedFrom":sQuery(id+"F11.wireOp",EDGE,"E69.bottom")}),1.0]])]});
            var Q20;
            Q20=makeQuery(id+"F11.imprint","IMPRINT",FACE,{"disambiguationData":[TD([[makeQuery(id+"F11.imprint","IMPRINT",EDGE,{"derivedFrom":sQuery(id+"F11.wireOp",EDGE,"E19.bottom")}),-1.0]])]});
            var Q21;
            Q21=makeQuery(id+"F11.imprint","IMPRINT",FACE,{"disambiguationData":[TD([[makeQuery(id+"F11.imprint","IMPRINT",EDGE,{"derivedFrom":sQuery(id+"F11.wireOp",EDGE,"E20.top")}),-1.0]])]});
            var Q22;
            Q22=makeQuery(id+"F11.imprint","IMPRINT",FACE,{"disambiguationData":[TD([[makeQuery(id+"F11.imprint","IMPRINT",EDGE,{"derivedFrom":sQuery(id+"F11.wireOp",EDGE,"E30.bottom")}),-1.0]])]});
            var Q23;
            Q23=makeQuery(id+"F11.imprint","IMPRINT",FACE,{"disambiguationData":[TD([[makeQuery(id+"F11.imprint","IMPRINT",EDGE,{"derivedFrom":sQuery(id+"F11.wireOp",EDGE,"E60.top")}),-1.0]])]});
            var Q24;
            Q24=makeQuery(id+"F11.imprint","IMPRINT",FACE,{"disambiguationData":[TD([[makeQuery(id+"F11.imprint","IMPRINT",EDGE,{"derivedFrom":sQuery(id+"F11.wireOp",EDGE,"E71.bottom")}),1.0]])]});
            var Q25;
            Q25=makeQuery(id+"F11.imprint","IMPRINT",FACE,{"disambiguationData":[TD([[makeQuery(id+"F11.imprint","IMPRINT",EDGE,{"derivedFrom":sQuery(id+"F11.wireOp",EDGE,"E43.top")}),-1.0]])]});
            var Q26;
            Q26=makeQuery(id+"F11.imprint","IMPRINT",FACE,{"disambiguationData":[TD([[makeQuery(id+"F11.imprint","IMPRINT",EDGE,{"derivedFrom":sQuery(id+"F11.wireOp",EDGE,"E44.top")}),1.0]])]});
            var Q27;
            Q27=makeQuery(id+"F11.imprint","IMPRINT",FACE,{"disambiguationData":[TD([[makeQuery(id+"F11.imprint","IMPRINT",EDGE,{"derivedFrom":sQuery(id+"F11.wireOp",EDGE,"E32.bottom")}),-1.0]])]});
            var Q28;
            Q28=makeQuery(id+"F11.imprint","IMPRINT",FACE,{"disambiguationData":[TD([[makeQuery(id+"F11.imprint","IMPRINT",EDGE,{"derivedFrom":sQuery(id+"F11.wireOp",EDGE,"E21.bottom")}),-1.0]])]});
            var Q29;
            Q29=makeQuery(id+"F11.imprint","IMPRINT",FACE,{"disambiguationData":[TD([[makeQuery(id+"F11.imprint","IMPRINT",EDGE,{"derivedFrom":sQuery(id+"F11.wireOp",EDGE,"E22.top")}),-1.0]])]});
            extrude(context, id + "F13", {"entities" : qUnion([Q0, Q1, Q2, Q3, Q4, Q5, Q6, Q7, Q8, Q9, Q10, Q11, Q12, Q13, Q14, Q15, Q16, Q17, Q18, Q19, Q20, Q21, Q22, Q23, Q24, Q25, Q26, Q27, Q28, Q29]), "operationType" : NewBodyOperationType.ADD, "depth" : 25.4 * mm, "hasDraft" : true, "draftAngle" : 35 * degree, "draftPullDirection" : true});
        }
        {
            var Q0;
            Q0 = qSketchRegion(id + "F4", true);
            extrude(context, id + "F14", {"entities" : qUnion([Q0]), "operationType" : NewBodyOperationType.ADD, "depth" : 127 * mm});
        }
        {
            var Q0;
            Q0=makeQuery(id+"F10.boolean.opBoolean","MERGE",FACE,{"derivedFrom":[makeQuery(id+"F5.boolean.opBoolean","MERGE",FACE,{"derivedFrom":[makeQuery(id+"F3.boolean.opBoolean","MERGE",FACE,{"derivedFrom":[makeQuery(id+"F1.opExtrude","SWEPT_FACE",FACE,{"disambiguationData":[OSD([sQuery(id+"F0.wireOp",EDGE,"E0.right")])]}),makeQuery(id+"F3.opExtrude","SWEPT_FACE",FACE,{"disambiguationData":[OSD([sQuery(id+"F2.wireOp",EDGE,"E2.left")])]})]}),makeQuery(id+"F5.opExtrude","SWEPT_FACE",FACE,{"disambiguationData":[OSD([sQuery(id+"F4.wireOp",EDGE,"E6.left")])]})]}),makeQuery(id+"F10.opExtrude","SWEPT_FACE",FACE,{"disambiguationData":[OSD([sQuery(id+"F9.wireOp",EDGE,"E9.right")])]})]});
            var sketch = newSketch(context, id + "F15", { "sketchPlane" : qUnion([Q0])});
            skCircle(sketch, "E73", {"center": v(-101.6, 127) * mm, "radius": 19.05 * mm});
            skCircle(sketch, "E74", {"center": v(25.4, 127) * mm, "radius": 19.05 * mm});
            skSolve(sketch);
        }
        {
            var Q0;
            Q0=sQuery(id+"F15.wireOp",VERTEX,"E73.center");
            var Q1;
            Q1=sQuery(id+"F15.wireOp",VERTEX,"E74.center");
            var Q2;
            Q2=makeQuery(id+"F1.opExtrude","SWEPT_BODY",BODY,{"disambiguationData":[OSD([sQuery(id+"F0.wireOp",EDGE,"E0.bottom"),sQuery(id+"F0.wireOp",EDGE,"E0.top"),sQuery(id+"F0.wireOp",EDGE,"E0.left"),sQuery(id+"F0.wireOp",EDGE,"E0.right")])]});
            hole(context, id + "F16", {"style" : HoleStyle.SIMPLE, "endStyle" : HoleEndStyle.THROUGH, "holeDiameter" : 38.1 * mm, "isTappedThrough" : true, "tappedDepth" : 12.7 * mm, "tapClearance" : 3, "locations" : qUnion([Q0, Q1]), "scope" : qUnion([Q2])});
        }
        {
            var Q0;
            Q0=makeQuery(id+"F10.boolean.opBoolean","MERGE",EDGE,{"derivedFrom":[makeQuery(id+"F5.opExtrude","CAP_EDGE",EDGE,{"disambiguationData":[OSD([sQuery(id+"F4.wireOp",EDGE,"E5.right")])],"isStart":false}),makeQuery(id+"F10.opExtrude","SWEPT_EDGE",EDGE,{"disambiguationData":[OSD([sQuery(id+"F9.wireOp",EDGE,"E9.bottom"),sQuery(id+"F9.wireOp",EDGE,"E9.left")])]})]});
            var Q1;
            Q1=makeQuery(id+"F5.opExtrude","SWEPT_EDGE",EDGE,{"disambiguationData":[OSD([sQuery(id+"F2.wireOp",EDGE,"E1.left"),sQuery(id+"F4.wireOp",EDGE,"E5.bottom"),sQuery(id+"F4.wireOp",EDGE,"E5.right")])]});
            var Q2;
            Q2=makeQuery(id+"F5.opExtrude","SWEPT_EDGE",EDGE,{"disambiguationData":[OSD([sQuery(id+"F2.wireOp",EDGE,"E2.left"),sQuery(id+"F4.wireOp",EDGE,"E6.top"),sQuery(id+"F4.wireOp",EDGE,"E6.left")])]});
            var Q3;
            Q3=makeQuery(id+"F10.boolean.opBoolean","MERGE",EDGE,{"derivedFrom":[makeQuery(id+"F5.opExtrude","CAP_EDGE",EDGE,{"disambiguationData":[OSD([sQuery(id+"F4.wireOp",EDGE,"E6.left")])],"isStart":false}),makeQuery(id+"F10.opExtrude","SWEPT_EDGE",EDGE,{"disambiguationData":[OSD([sQuery(id+"F9.wireOp",EDGE,"E9.bottom"),sQuery(id+"F9.wireOp",EDGE,"E9.right")])]})]});
            var Q4;
            Q4=makeQuery(id+"F10.opExtrude","CAP_EDGE",EDGE,{"disambiguationData":[OSD([sQuery(id+"F9.wireOp",EDGE,"E9.bottom")])],"isStart":false});
            chamfer(context, id + "F17", {"entities" : qUnion([Q0, Q1, Q2, Q3, Q4]), "width" : 25.4 * mm, "tangentPropagation" : true});
        }
        {
            var Q0;
            {var subQ0=sQuery(id+"F0.wireOp",EDGE,"E0.bottom");Q0=makeQuery(id+"F10.boolean.opBoolean","MERGE",FACE,{"derivedFrom":[makeQuery(id+"F7.boolean.opBoolean","MERGE",FACE,{"derivedFrom":[makeQuery(id+"F1.opExtrude","CAP_FACE",FACE,{"disambiguationData":[OSD([subQ0,sQuery(id+"F0.wireOp",EDGE,"E0.top"),sQuery(id+"F0.wireOp",EDGE,"E0.left"),sQuery(id+"F0.wireOp",EDGE,"E0.right")])],"isStart":true}),makeQuery(id+"F7.opExtrude","CAP_FACE",FACE,{"disambiguationData":[OSD([subQ0,sQuery(id+"F6.wireOp",EDGE,"E7"),sQuery(id+"F6.wireOp",EDGE,"E8")])],"isStart":true})]}),makeQuery(id+"F10.opExtrude","SWEPT_FACE",FACE,{"disambiguationData":[OSD([sQuery(id+"F9.wireOp",EDGE,"E9.top")])]})]});}
            var sketch = newSketch(context, id + "F18", { "sketchPlane" : qUnion([Q0])});
            skLineSegment(sketch, "E75.bottom", {"start": v(-152.4, 152.4) * mm, "end": v(152.4, 152.4) * mm});
            skLineSegment(sketch, "E75.top", {"start": v(-152.4, 101.6) * mm, "end": v(152.4, 101.6) * mm});
            skLineSegment(sketch, "E75.left", {"start": v(-152.4, 152.4) * mm, "end": v(-152.4, 101.6) * mm});
            skLineSegment(sketch, "E75.right", {"start": v(152.4, 152.4) * mm, "end": v(152.4, 101.6) * mm});
            skLineSegment(sketch, "E76.bottom", {"start": v(152.4, 101.6) * mm, "end": v(101.6, 101.6) * mm});
            skLineSegment(sketch, "E76.top", {"start": v(152.4, -152.4) * mm, "end": v(101.6, -152.4) * mm});
            skLineSegment(sketch, "E76.left", {"start": v(152.4, 101.6) * mm, "end": v(152.4, -152.4) * mm});
            skLineSegment(sketch, "E76.right", {"start": v(101.6, 101.6) * mm, "end": v(101.6, -152.4) * mm});
            skLineSegment(sketch, "E77.bottom", {"start": v(-152.4, 101.6) * mm, "end": v(-101.6, 101.6) * mm});
            skLineSegment(sketch, "E77.top", {"start": v(-152.4, -152.4) * mm, "end": v(-101.6, -152.4) * mm});
            skLineSegment(sketch, "E77.left", {"start": v(-152.4, 101.6) * mm, "end": v(-152.4, -152.4) * mm});
            skLineSegment(sketch, "E77.right", {"start": v(-101.6, 101.6) * mm, "end": v(-101.6, -152.4) * mm});
            skLineSegment(sketch, "E78.bottom", {"start": v(-101.6, -152.4) * mm, "end": v(101.6, -152.4) * mm});
            skLineSegment(sketch, "E78.top", {"start": v(-101.6, -101.6) * mm, "end": v(101.6, -101.6) * mm});
            skLineSegment(sketch, "E78.left", {"start": v(-101.6, -152.4) * mm, "end": v(-101.6, -101.6) * mm});
            skLineSegment(sketch, "E78.right", {"start": v(101.6, -152.4) * mm, "end": v(101.6, -101.6) * mm});
            skSolve(sketch);
        }
        {
            var Q0;
            Q0 = qSketchRegion(id + "F18", true);
            extrude(context, id + "F19", {"entities" : qUnion([Q0]), "operationType" : NewBodyOperationType.ADD, "depth" : 50.8 * mm});
        }
        {
            var Q0;
            {var subQ0=sQuery(id+"F6.wireOp",EDGE,"E8");var subQ1=sQuery(id+"F6.wireOp",EDGE,"E7");var subQ2=sQuery(id+"F0.wireOp",EDGE,"E0.left");var subQ3=sQuery(id+"F0.wireOp",EDGE,"E0.right");var subQ4=sQuery(id+"F0.wireOp",EDGE,"E0.bottom");Q0=makeQuery(id+"F19.boolean.opBoolean","SPLIT",FACE,{"disambiguationData":[TD([makeQuery(id+"F1.opExtrude","SWEPT_FACE",FACE,{"disambiguationData":[OSD([subQ2])]})])],"derivedFrom":makeQuery(id+"F10.boolean.opBoolean","MERGE",FACE,{"derivedFrom":[makeQuery(id+"F7.boolean.opBoolean","MERGE",FACE,{"derivedFrom":[makeQuery(id+"F1.opExtrude","CAP_FACE",FACE,{"disambiguationData":[OSD([subQ4,sQuery(id+"F0.wireOp",EDGE,"E0.top"),subQ2,subQ3])],"isStart":true}),makeQuery(id+"F7.opExtrude","CAP_FACE",FACE,{"disambiguationData":[OSD([subQ4,subQ1,subQ0])],"isStart":true})]}),makeQuery(id+"F10.opExtrude","SWEPT_FACE",FACE,{"disambiguationData":[OSD([sQuery(id+"F9.wireOp",EDGE,"E9.top")])]})]})});}
            var sketch = newSketch(context, id + "F20", { "sketchPlane" : qUnion([Q0])});
            skLineSegment(sketch, "E79", {"start": v(152.4, -152.4) * mm, "end": v(0, -295.16) * mm});
            skLineSegment(sketch, "E80", {"start": v(0, -295.16) * mm, "end": v(-152.4, -152.4) * mm});
            skLineSegment(sketch, "E81", {"start": v(-152.4, -152.4) * mm, "end": v(152.4, -152.4) * mm});
            skSolve(sketch);
        }
        {
            var Q0;
            Q0 = qSketchRegion(id + "F20", true);
            extrude(context, id + "F21", {"entities" : qUnion([Q0]), "operationType" : NewBodyOperationType.ADD, "depth" : 50.8 * mm});
        }
        {
            var Q0;
            {var subQ0=sQuery(id+"F6.wireOp",EDGE,"E7");var subQ1=sQuery(id+"F0.wireOp",EDGE,"E0.bottom");Q0=makeQuery(id+"F21.boolean.opBoolean","MERGE",EDGE,{"derivedFrom":[makeQuery(id+"F8.opChamfer","BLEND_EDGE",EDGE,{"blendedFrom":[makeQuery(id+"F7.opExtrude","CAP_EDGE",EDGE,{"disambiguationData":[OSD([subQ0])],"isStart":false}),makeQuery(id+"F7.boolean.opBoolean","MERGE",FACE,{"derivedFrom":[makeQuery(id+"F1.opExtrude","CAP_FACE",FACE,{"disambiguationData":[OSD([subQ1,sQuery(id+"F0.wireOp",EDGE,"E0.top"),sQuery(id+"F0.wireOp",EDGE,"E0.left"),sQuery(id+"F0.wireOp",EDGE,"E0.right")])],"isStart":true}),makeQuery(id+"F7.opExtrude","CAP_FACE",FACE,{"disambiguationData":[OSD([subQ1,subQ0,sQuery(id+"F6.wireOp",EDGE,"E8")])],"isStart":true})]})],"blendedInto":[makeQuery(id+"F7.boolean.opBoolean","MERGE",FACE,{"derivedFrom":[makeQuery(id+"F1.opExtrude","CAP_FACE",FACE,{"disambiguationData":[OSD([subQ1,sQuery(id+"F0.wireOp",EDGE,"E0.top"),sQuery(id+"F0.wireOp",EDGE,"E0.left"),sQuery(id+"F0.wireOp",EDGE,"E0.right")])],"isStart":true}),makeQuery(id+"F7.opExtrude","CAP_FACE",FACE,{"disambiguationData":[OSD([subQ1,subQ0,sQuery(id+"F6.wireOp",EDGE,"E8")])],"isStart":true})]})]}),makeQuery(id+"F21.opExtrude","CAP_EDGE",EDGE,{"disambiguationData":[OSD([sQuery(id+"F20.wireOp",EDGE,"E79")])],"isStart":true})]});}
            var Q1;
            {var subQ0=sQuery(id+"F6.wireOp",EDGE,"E8");var subQ1=sQuery(id+"F0.wireOp",EDGE,"E0.bottom");Q1=makeQuery(id+"F21.boolean.opBoolean","MERGE",EDGE,{"derivedFrom":[makeQuery(id+"F8.opChamfer","BLEND_EDGE",EDGE,{"blendedFrom":[makeQuery(id+"F7.opExtrude","CAP_EDGE",EDGE,{"disambiguationData":[OSD([subQ0])],"isStart":false}),makeQuery(id+"F7.boolean.opBoolean","MERGE",FACE,{"derivedFrom":[makeQuery(id+"F1.opExtrude","CAP_FACE",FACE,{"disambiguationData":[OSD([subQ1,sQuery(id+"F0.wireOp",EDGE,"E0.top"),sQuery(id+"F0.wireOp",EDGE,"E0.left"),sQuery(id+"F0.wireOp",EDGE,"E0.right")])],"isStart":true}),makeQuery(id+"F7.opExtrude","CAP_FACE",FACE,{"disambiguationData":[OSD([subQ1,sQuery(id+"F6.wireOp",EDGE,"E7"),subQ0])],"isStart":true})]})],"blendedInto":[makeQuery(id+"F7.boolean.opBoolean","MERGE",FACE,{"derivedFrom":[makeQuery(id+"F1.opExtrude","CAP_FACE",FACE,{"disambiguationData":[OSD([subQ1,sQuery(id+"F0.wireOp",EDGE,"E0.top"),sQuery(id+"F0.wireOp",EDGE,"E0.left"),sQuery(id+"F0.wireOp",EDGE,"E0.right")])],"isStart":true}),makeQuery(id+"F7.opExtrude","CAP_FACE",FACE,{"disambiguationData":[OSD([subQ1,sQuery(id+"F6.wireOp",EDGE,"E7"),subQ0])],"isStart":true})]})]}),makeQuery(id+"F21.opExtrude","CAP_EDGE",EDGE,{"disambiguationData":[OSD([sQuery(id+"F20.wireOp",EDGE,"E80")])],"isStart":true})]});}
            chamfer(context, id + "F22", {"entities" : qUnion([Q0, Q1]), "width" : 50.8 * mm, "tangentPropagation" : true});
        }
        {
            var Q0;
            Q0=makeQuery(id+"F19.opExtrude","SWEPT_FACE",FACE,{"disambiguationData":[OSD([sQuery(id+"F18.wireOp",EDGE,"E75.bottom")])]});
            var sketch = newSketch(context, id + "F23", { "sketchPlane" : qUnion([Q0])});
            skLineSegment(sketch, "E82.bottom", {"start": v(-152.4, 0) * mm, "end": v(152.4, 0) * mm});
            skLineSegment(sketch, "E82.top", {"start": v(-152.4, -50.8) * mm, "end": v(152.4, -50.8) * mm});
            skLineSegment(sketch, "E82.left", {"start": v(-152.4, 0) * mm, "end": v(-152.4, -50.8) * mm});
            skLineSegment(sketch, "E82.right", {"start": v(152.4, 0) * mm, "end": v(152.4, -50.8) * mm});
            skSolve(sketch);
        }
        {
            var Q0;
            Q0 = qSketchRegion(id + "F23", true);
            extrude(context, id + "F24", {"entities" : qUnion([Q0]), "operationType" : NewBodyOperationType.ADD, "depth" : 25.4 * mm});
        }
        {
            var Q0;
            {var subQ0=sQuery(id+"F9.wireOp",EDGE,"E9.left");var subQ1=sQuery(id+"F9.wireOp",EDGE,"E9.top");var subQ2=sQuery(id+"F9.wireOp",EDGE,"E9.right");var subQ3=sQuery(id+"F9.wireOp",EDGE,"E9.bottom");var subQ4=makeQuery(id+"F10.opExtrude","CAP_FACE",FACE,{"disambiguationData":[OSD([subQ3,subQ1,subQ0,subQ2])],"isStart":false});var subQ5=sQuery(id+"F0.wireOp",EDGE,"E0.bottom");var subQ6=sQuery(id+"F4.wireOp",EDGE,"E6.left");var subQ7=sQuery(id+"F4.wireOp",EDGE,"E5.right");var subQ8=sQuery(id+"F0.wireOp",EDGE,"E0.right");var subQ9=sQuery(id+"F0.wireOp",EDGE,"E0.left");Q0=makeQuery(id+"F24.boolean.opBoolean","MERGE",FACE,{"derivedFrom":[makeQuery(id+"F12.boolean.opBoolean","SPLIT",FACE,{"disambiguationData":[TD([makeQuery(id+"F1.opExtrude","CAP_FACE",FACE,{"disambiguationData":[OSD([subQ5,sQuery(id+"F0.wireOp",EDGE,"E0.top"),subQ9,subQ8])],"isStart":true}),makeQuery(id+"F1.opExtrude","SWEPT_FACE",FACE,{"disambiguationData":[OSD([subQ9])]}),makeQuery(id+"F1.opExtrude","SWEPT_FACE",FACE,{"disambiguationData":[OSD([subQ8])]}),makeQuery(id+"F3.opExtrude","SWEPT_FACE",FACE,{"disambiguationData":[OSD([sQuery(id+"F2.wireOp",EDGE,"E1.left")])]}),makeQuery(id+"F3.opExtrude","SWEPT_FACE",FACE,{"disambiguationData":[OSD([sQuery(id+"F2.wireOp",EDGE,"E2.left")])]}),makeQuery(id+"F5.opExtrude","CAP_FACE",FACE,{"disambiguationData":[OSD([sQuery(id+"F4.wireOp",EDGE,"E5.bottom"),sQuery(id+"F4.wireOp",EDGE,"E5.top"),sQuery(id+"F4.wireOp",EDGE,"E5.left"),subQ7])],"isStart":false}),makeQuery(id+"F5.opExtrude","SWEPT_FACE",FACE,{"disambiguationData":[OSD([subQ7])]}),makeQuery(id+"F5.opExtrude","CAP_FACE",FACE,{"disambiguationData":[OSD([sQuery(id+"F4.wireOp",EDGE,"E6.bottom"),sQuery(id+"F4.wireOp",EDGE,"E6.top"),subQ6,sQuery(id+"F4.wireOp",EDGE,"E6.right")])],"isStart":false}),makeQuery(id+"F5.opExtrude","SWEPT_FACE",FACE,{"disambiguationData":[OSD([subQ6])]}),makeQuery(id+"F7.opExtrude","CAP_FACE",FACE,{"disambiguationData":[OSD([subQ5,sQuery(id+"F6.wireOp",EDGE,"E7"),sQuery(id+"F6.wireOp",EDGE,"E8")])],"isStart":true}),makeQuery(id+"F10.opExtrude","SWEPT_FACE",FACE,{"disambiguationData":[OSD([subQ3])]}),subQ4,makeQuery(id+"F10.opExtrude","SWEPT_FACE",FACE,{"disambiguationData":[OSD([subQ1])]}),makeQuery(id+"F10.opExtrude","SWEPT_FACE",FACE,{"disambiguationData":[OSD([subQ0])]}),makeQuery(id+"F10.opExtrude","SWEPT_FACE",FACE,{"disambiguationData":[OSD([subQ2])]}),makeQuery(id+"F12.opExtrude","SWEPT_FACE",FACE,{"disambiguationData":[OSD([sQuery(id+"F11.wireOp",EDGE,"E13.bottom")])]}),makeQuery(id+"F12.opExtrude","SWEPT_FACE",FACE,{"disambiguationData":[OSD([sQuery(id+"F11.wireOp",EDGE,"E13.left")])]}),makeQuery(id+"F12.opExtrude","SWEPT_FACE",FACE,{"disambiguationData":[OSD([sQuery(id+"F11.wireOp",EDGE,"E14.left")])]}),makeQuery(id+"F12.opExtrude","SWEPT_FACE",FACE,{"disambiguationData":[OSD([sQuery(id+"F11.wireOp",EDGE,"E15.top")])]}),makeQuery(id+"F12.opExtrude","SWEPT_FACE",FACE,{"disambiguationData":[OSD([sQuery(id+"F11.wireOp",EDGE,"E14.right")])]}),makeQuery(id+"F12.opExtrude","SWEPT_FACE",FACE,{"disambiguationData":[OSD([sQuery(id+"F11.wireOp",EDGE,"E15.right")])]}),makeQuery(id+"F12.opExtrude","SWEPT_FACE",FACE,{"disambiguationData":[OSD([sQuery(id+"F11.wireOp",EDGE,"E17.top")])]}),makeQuery(id+"F12.opExtrude","SWEPT_FACE",FACE,{"disambiguationData":[OSD([sQuery(id+"F11.wireOp",EDGE,"E16.right")])]}),makeQuery(id+"F12.opExtrude","SWEPT_FACE",FACE,{"disambiguationData":[OSD([sQuery(id+"F11.wireOp",EDGE,"E17.right")])]}),makeQuery(id+"F12.opExtrude","SWEPT_FACE",FACE,{"disambiguationData":[OSD([sQuery(id+"F11.wireOp",EDGE,"E19.top")])]}),makeQuery(id+"F12.opExtrude","SWEPT_FACE",FACE,{"disambiguationData":[OSD([sQuery(id+"F11.wireOp",EDGE,"E18.right")])]}),makeQuery(id+"F12.opExtrude","SWEPT_FACE",FACE,{"disambiguationData":[OSD([sQuery(id+"F11.wireOp",EDGE,"E19.right")])]}),makeQuery(id+"F12.opExtrude","SWEPT_FACE",FACE,{"disambiguationData":[OSD([sQuery(id+"F11.wireOp",EDGE,"E21.top")])]}),makeQuery(id+"F12.opExtrude","SWEPT_FACE",FACE,{"disambiguationData":[OSD([sQuery(id+"F11.wireOp",EDGE,"E20.right")])]}),makeQuery(id+"F12.opExtrude","SWEPT_FACE",FACE,{"disambiguationData":[OSD([sQuery(id+"F11.wireOp",EDGE,"E21.right")])]}),makeQuery(id+"F12.opExtrude","SWEPT_FACE",FACE,{"disambiguationData":[OSD([sQuery(id+"F11.wireOp",EDGE,"E13.top")])]}),makeQuery(id+"F12.opExtrude","SWEPT_FACE",FACE,{"disambiguationData":[OSD([sQuery(id+"F11.wireOp",EDGE,"E14.bottom")])]}),makeQuery(id+"F12.opExtrude","SWEPT_FACE",FACE,{"disambiguationData":[OSD([sQuery(id+"F11.wireOp",EDGE,"E24.left")])]}),makeQuery(id+"F12.opExtrude","SWEPT_FACE",FACE,{"disambiguationData":[OSD([sQuery(id+"F11.wireOp",EDGE,"E15.bottom")])]}),makeQuery(id+"F12.opExtrude","SWEPT_FACE",FACE,{"disambiguationData":[OSD([sQuery(id+"F11.wireOp",EDGE,"E24.right")])]}),makeQuery(id+"F12.opExtrude","SWEPT_FACE",FACE,{"disambiguationData":[OSD([sQuery(id+"F11.wireOp",EDGE,"E16.bottom")])]}),makeQuery(id+"F12.opExtrude","SWEPT_FACE",FACE,{"disambiguationData":[OSD([sQuery(id+"F11.wireOp",EDGE,"E25.right")])]}),makeQuery(id+"F12.opExtrude","SWEPT_FACE",FACE,{"disambiguationData":[OSD([sQuery(id+"F11.wireOp",EDGE,"E17.bottom")])]}),makeQuery(id+"F12.opExtrude","SWEPT_FACE",FACE,{"disambiguationData":[OSD([sQuery(id+"F11.wireOp",EDGE,"E26.right")])]}),makeQuery(id+"F12.opExtrude","SWEPT_FACE",FACE,{"disambiguationData":[OSD([sQuery(id+"F11.wireOp",EDGE,"E18.bottom")])]}),makeQuery(id+"F12.opExtrude","SWEPT_FACE",FACE,{"disambiguationData":[OSD([sQuery(id+"F11.wireOp",EDGE,"E27.right")])]}),makeQuery(id+"F12.opExtrude","SWEPT_FACE",FACE,{"disambiguationData":[OSD([sQuery(id+"F11.wireOp",EDGE,"E19.bottom")])]}),makeQuery(id+"F12.opExtrude","SWEPT_FACE",FACE,{"disambiguationData":[OSD([sQuery(id+"F11.wireOp",EDGE,"E28.right")])]}),makeQuery(id+"F12.opExtrude","SWEPT_FACE",FACE,{"disambiguationData":[OSD([sQuery(id+"F11.wireOp",EDGE,"E20.bottom")])]}),makeQuery(id+"F12.opExtrude","SWEPT_FACE",FACE,{"disambiguationData":[OSD([sQuery(id+"F11.wireOp",EDGE,"E29.right")])]}),makeQuery(id+"F12.opExtrude","SWEPT_FACE",FACE,{"disambiguationData":[OSD([sQuery(id+"F11.wireOp",EDGE,"E21.bottom")])]}),makeQuery(id+"F12.opExtrude","SWEPT_FACE",FACE,{"disambiguationData":[OSD([sQuery(id+"F11.wireOp",EDGE,"E30.right")])]}),makeQuery(id+"F12.opExtrude","SWEPT_FACE",FACE,{"disambiguationData":[OSD([sQuery(id+"F11.wireOp",EDGE,"E22.bottom")])]}),makeQuery(id+"F12.opExtrude","SWEPT_FACE",FACE,{"disambiguationData":[OSD([sQuery(id+"F11.wireOp",EDGE,"E31.right")])]}),makeQuery(id+"F12.opExtrude","SWEPT_FACE",FACE,{"disambiguationData":[OSD([sQuery(id+"F11.wireOp",EDGE,"E32.right")])]}),makeQuery(id+"F12.opExtrude","SWEPT_FACE",FACE,{"disambiguationData":[OSD([sQuery(id+"F11.wireOp",EDGE,"E23.top")])]}),makeQuery(id+"F12.opExtrude","SWEPT_FACE",FACE,{"disambiguationData":[OSD([sQuery(id+"F11.wireOp",EDGE,"E33.left")])]}),makeQuery(id+"F12.opExtrude","SWEPT_FACE",FACE,{"disambiguationData":[OSD([sQuery(id+"F11.wireOp",EDGE,"E24.bottom")])]}),makeQuery(id+"F12.opExtrude","SWEPT_FACE",FACE,{"disambiguationData":[OSD([sQuery(id+"F11.wireOp",EDGE,"E34.left")])]}),makeQuery(id+"F12.opExtrude","SWEPT_FACE",FACE,{"disambiguationData":[OSD([sQuery(id+"F11.wireOp",EDGE,"E31.bottom")])]}),makeQuery(id+"F12.opExtrude","SWEPT_FACE",FACE,{"disambiguationData":[OSD([sQuery(id+"F11.wireOp",EDGE,"E32.bottom")])]}),makeQuery(id+"F12.opExtrude","SWEPT_FACE",FACE,{"disambiguationData":[OSD([sQuery(id+"F11.wireOp",EDGE,"E41.right")])]}),makeQuery(id+"F12.opExtrude","SWEPT_FACE",FACE,{"disambiguationData":[OSD([sQuery(id+"F11.wireOp",EDGE,"E42.bottom")])]}),makeQuery(id+"F12.opExtrude","SWEPT_FACE",FACE,{"disambiguationData":[OSD([sQuery(id+"F11.wireOp",EDGE,"E43.right")])]}),makeQuery(id+"F12.opExtrude","SWEPT_FACE",FACE,{"disambiguationData":[OSD([sQuery(id+"F11.wireOp",EDGE,"E44.top")])]}),makeQuery(id+"F12.opExtrude","SWEPT_FACE",FACE,{"disambiguationData":[OSD([sQuery(id+"F11.wireOp",EDGE,"E44.left")])]}),makeQuery(id+"F12.opExtrude","SWEPT_FACE",FACE,{"disambiguationData":[OSD([sQuery(id+"F11.wireOp",EDGE,"E34.bottom")])]}),makeQuery(id+"F12.opExtrude","SWEPT_FACE",FACE,{"disambiguationData":[OSD([sQuery(id+"F11.wireOp",EDGE,"E33.top")])]}),makeQuery(id+"F12.opExtrude","SWEPT_FACE",FACE,{"disambiguationData":[OSD([sQuery(id+"F11.wireOp",EDGE,"E51.left")])]}),makeQuery(id+"F12.opExtrude","SWEPT_FACE",FACE,{"disambiguationData":[OSD([sQuery(id+"F11.wireOp",EDGE,"E52.top")])]}),makeQuery(id+"F12.opExtrude","SWEPT_FACE",FACE,{"disambiguationData":[OSD([sQuery(id+"F11.wireOp",EDGE,"E53.left")])]}),makeQuery(id+"F12.opExtrude","SWEPT_FACE",FACE,{"disambiguationData":[OSD([sQuery(id+"F11.wireOp",EDGE,"E51.top")])]}),makeQuery(id+"F12.opExtrude","SWEPT_FACE",FACE,{"disambiguationData":[OSD([sQuery(id+"F11.wireOp",EDGE,"E54.left")])]}),makeQuery(id+"F12.opExtrude","SWEPT_FACE",FACE,{"disambiguationData":[OSD([sQuery(id+"F11.wireOp",EDGE,"E54.right")])]}),makeQuery(id+"F12.opExtrude","SWEPT_FACE",FACE,{"disambiguationData":[OSD([sQuery(id+"F11.wireOp",EDGE,"E55.right")])]}),makeQuery(id+"F12.opExtrude","SWEPT_FACE",FACE,{"disambiguationData":[OSD([sQuery(id+"F11.wireOp",EDGE,"E56.right")])]}),makeQuery(id+"F12.opExtrude","SWEPT_FACE",FACE,{"disambiguationData":[OSD([sQuery(id+"F11.wireOp",EDGE,"E57.right")])]}),makeQuery(id+"F12.opExtrude","SWEPT_FACE",FACE,{"disambiguationData":[OSD([sQuery(id+"F11.wireOp",EDGE,"E58.right")])]}),makeQuery(id+"F12.opExtrude","SWEPT_FACE",FACE,{"disambiguationData":[OSD([sQuery(id+"F11.wireOp",EDGE,"E59.right")])]}),makeQuery(id+"F12.opExtrude","SWEPT_FACE",FACE,{"disambiguationData":[OSD([sQuery(id+"F11.wireOp",EDGE,"E61.top")])]}),makeQuery(id+"F12.opExtrude","SWEPT_FACE",FACE,{"disambiguationData":[OSD([sQuery(id+"F11.wireOp",EDGE,"E60.right")])]}),makeQuery(id+"F12.opExtrude","SWEPT_FACE",FACE,{"disambiguationData":[OSD([sQuery(id+"F11.wireOp",EDGE,"E43.top")])]}),makeQuery(id+"F12.opExtrude","SWEPT_FACE",FACE,{"disambiguationData":[OSD([sQuery(id+"F11.wireOp",EDGE,"E61.right")])]}),makeQuery(id+"F12.opExtrude","SWEPT_FACE",FACE,{"disambiguationData":[OSD([sQuery(id+"F11.wireOp",EDGE,"E53.top")])]}),makeQuery(id+"F12.opExtrude","SWEPT_FACE",FACE,{"disambiguationData":[OSD([sQuery(id+"F11.wireOp",EDGE,"E54.bottom")])]}),makeQuery(id+"F12.opExtrude","SWEPT_FACE",FACE,{"disambiguationData":[OSD([sQuery(id+"F11.wireOp",EDGE,"E64.top")])]}),makeQuery(id+"F12.opExtrude","SWEPT_FACE",FACE,{"disambiguationData":[OSD([sQuery(id+"F11.wireOp",EDGE,"E63.right")])]}),makeQuery(id+"F12.opExtrude","SWEPT_FACE",FACE,{"disambiguationData":[OSD([sQuery(id+"F11.wireOp",EDGE,"E55.bottom")])]}),makeQuery(id+"F12.opExtrude","SWEPT_FACE",FACE,{"disambiguationData":[OSD([sQuery(id+"F11.wireOp",EDGE,"E65.left")])]}),makeQuery(id+"F12.opExtrude","SWEPT_FACE",FACE,{"disambiguationData":[OSD([sQuery(id+"F11.wireOp",EDGE,"E66.bottom")])]}),makeQuery(id+"F12.opExtrude","SWEPT_FACE",FACE,{"disambiguationData":[OSD([sQuery(id+"F11.wireOp",EDGE,"E56.bottom")])]}),makeQuery(id+"F12.opExtrude","SWEPT_FACE",FACE,{"disambiguationData":[OSD([sQuery(id+"F11.wireOp",EDGE,"E65.right")])]}),makeQuery(id+"F12.opExtrude","SWEPT_FACE",FACE,{"disambiguationData":[OSD([sQuery(id+"F11.wireOp",EDGE,"E57.bottom")])]}),makeQuery(id+"F12.opExtrude","SWEPT_FACE",FACE,{"disambiguationData":[OSD([sQuery(id+"F11.wireOp",EDGE,"E66.right")])]}),makeQuery(id+"F12.opExtrude","SWEPT_FACE",FACE,{"disambiguationData":[OSD([sQuery(id+"F11.wireOp",EDGE,"E68.bottom")])]}),makeQuery(id+"F12.opExtrude","SWEPT_FACE",FACE,{"disambiguationData":[OSD([sQuery(id+"F11.wireOp",EDGE,"E58.bottom")])]}),makeQuery(id+"F12.opExtrude","SWEPT_FACE",FACE,{"disambiguationData":[OSD([sQuery(id+"F11.wireOp",EDGE,"E67.right")])]}),makeQuery(id+"F12.opExtrude","SWEPT_FACE",FACE,{"disambiguationData":[OSD([sQuery(id+"F11.wireOp",EDGE,"E59.bottom")])]}),makeQuery(id+"F12.opExtrude","SWEPT_FACE",FACE,{"disambiguationData":[OSD([sQuery(id+"F11.wireOp",EDGE,"E68.right")])]}),makeQuery(id+"F12.opExtrude","SWEPT_FACE",FACE,{"disambiguationData":[OSD([sQuery(id+"F11.wireOp",EDGE,"E70.bottom")])]}),makeQuery(id+"F12.opExtrude","SWEPT_FACE",FACE,{"disambiguationData":[OSD([sQuery(id+"F11.wireOp",EDGE,"E60.bottom")])]}),makeQuery(id+"F12.opExtrude","SWEPT_FACE",FACE,{"disambiguationData":[OSD([sQuery(id+"F11.wireOp",EDGE,"E69.right")])]}),makeQuery(id+"F12.opExtrude","SWEPT_FACE",FACE,{"disambiguationData":[OSD([sQuery(id+"F11.wireOp",EDGE,"E61.bottom")])]}),makeQuery(id+"F12.opExtrude","SWEPT_FACE",FACE,{"disambiguationData":[OSD([sQuery(id+"F11.wireOp",EDGE,"E70.right")])]}),makeQuery(id+"F12.opExtrude","SWEPT_FACE",FACE,{"disambiguationData":[OSD([sQuery(id+"F11.wireOp",EDGE,"E72.bottom")])]}),makeQuery(id+"F12.opExtrude","SWEPT_FACE",FACE,{"disambiguationData":[OSD([sQuery(id+"F11.wireOp",EDGE,"E62.bottom")])]}),makeQuery(id+"F12.opExtrude","SWEPT_FACE",FACE,{"disambiguationData":[OSD([sQuery(id+"F11.wireOp",EDGE,"E71.right")])]}),makeQuery(id+"F12.opExtrude","SWEPT_FACE",FACE,{"disambiguationData":[OSD([sQuery(id+"F11.wireOp",EDGE,"E72.right")])]})])],"derivedFrom":subQ4}),makeQuery(id+"F24.opExtrude","CAP_FACE",FACE,{"disambiguationData":[OSD([sQuery(id+"F23.wireOp",EDGE,"E82.bottom"),sQuery(id+"F23.wireOp",EDGE,"E82.top"),sQuery(id+"F23.wireOp",EDGE,"E82.left"),sQuery(id+"F23.wireOp",EDGE,"E82.right")])],"isStart":false})]});}
            var sketch = newSketch(context, id + "F25", { "sketchPlane" : qUnion([Q0])});
            skLineSegment(sketch, "E83.bottom", {"start": v(-127, 25.4) * mm, "end": v(-101.6, 25.4) * mm});
            skLineSegment(sketch, "E83.top", {"start": v(-127, 0) * mm, "end": v(-101.6, 0) * mm});
            skLineSegment(sketch, "E83.left", {"start": v(-127, 25.4) * mm, "end": v(-127, 0) * mm});
            skLineSegment(sketch, "E83.right", {"start": v(-101.6, 25.4) * mm, "end": v(-101.6, 0) * mm});
            skLineSegment(sketch, "E84.bottom", {"start": v(-101.6, 0) * mm, "end": v(-76.2, 0) * mm});
            skLineSegment(sketch, "E84.top", {"start": v(-101.6, 25.4) * mm, "end": v(-76.2, 25.4) * mm});
            skLineSegment(sketch, "E84.left", {"start": v(-101.6, 0) * mm, "end": v(-101.6, 25.4) * mm});
            skLineSegment(sketch, "E84.right", {"start": v(-76.2, 0) * mm, "end": v(-76.2, 25.4) * mm});
            skLineSegment(sketch, "E85.bottom", {"start": v(-76.2, 0) * mm, "end": v(-50.8, 0) * mm});
            skLineSegment(sketch, "E85.top", {"start": v(-76.2, 25.4) * mm, "end": v(-50.8, 25.4) * mm});
            skLineSegment(sketch, "E85.right", {"start": v(-50.8, 0) * mm, "end": v(-50.8, 25.4) * mm});
            skLineSegment(sketch, "E86.bottom", {"start": v(-50.8, 0) * mm, "end": v(-25.4, 0) * mm});
            skLineSegment(sketch, "E86.top", {"start": v(-50.8, 25.4) * mm, "end": v(-25.4, 25.4) * mm});
            skLineSegment(sketch, "E86.right", {"start": v(-25.4, 0) * mm, "end": v(-25.4, 25.4) * mm});
            skLineSegment(sketch, "E87.bottom", {"start": v(-25.4, 0) * mm, "end": v(0, 0) * mm});
            skLineSegment(sketch, "E87.top", {"start": v(-25.4, 25.4) * mm, "end": v(0, 25.4) * mm});
            skLineSegment(sketch, "E87.right", {"start": v(0, 0) * mm, "end": v(0, 25.4) * mm});
            skLineSegment(sketch, "E88.bottom", {"start": v(0, 0) * mm, "end": v(25.4, 0) * mm});
            skLineSegment(sketch, "E88.top", {"start": v(0, 25.4) * mm, "end": v(25.4, 25.4) * mm});
            skLineSegment(sketch, "E88.right", {"start": v(25.4, 0) * mm, "end": v(25.4, 25.4) * mm});
            skLineSegment(sketch, "E89.bottom", {"start": v(25.4, 0) * mm, "end": v(50.8, 0) * mm});
            skLineSegment(sketch, "E89.top", {"start": v(25.4, 25.4) * mm, "end": v(50.8, 25.4) * mm});
            skLineSegment(sketch, "E89.right", {"start": v(50.8, 0) * mm, "end": v(50.8, 25.4) * mm});
            skLineSegment(sketch, "E90.bottom", {"start": v(50.8, 0) * mm, "end": v(76.2, 0) * mm});
            skLineSegment(sketch, "E90.top", {"start": v(50.8, 25.4) * mm, "end": v(76.2, 25.4) * mm});
            skLineSegment(sketch, "E90.right", {"start": v(76.2, 0) * mm, "end": v(76.2, 25.4) * mm});
            skLineSegment(sketch, "E91.bottom", {"start": v(76.2, 0) * mm, "end": v(101.6, 0) * mm});
            skLineSegment(sketch, "E91.top", {"start": v(76.2, 25.4) * mm, "end": v(101.6, 25.4) * mm});
            skLineSegment(sketch, "E91.right", {"start": v(101.6, 0) * mm, "end": v(101.6, 25.4) * mm});
            skLineSegment(sketch, "E92.bottom", {"start": v(101.6, 0) * mm, "end": v(127, 0) * mm});
            skLineSegment(sketch, "E92.top", {"start": v(101.6, 25.4) * mm, "end": v(127, 25.4) * mm});
            skLineSegment(sketch, "E92.right", {"start": v(127, 0) * mm, "end": v(127, 25.4) * mm});
            skLineSegment(sketch, "E93.bottom", {"start": v(-152.4, -50.8) * mm, "end": v(152.4, -50.8) * mm});
            skLineSegment(sketch, "E93.top", {"start": v(-152.4, -25.4) * mm, "end": v(152.4, -25.4) * mm});
            skLineSegment(sketch, "E93.left", {"start": v(-152.4, -50.8) * mm, "end": v(-152.4, -25.4) * mm});
            skLineSegment(sketch, "E93.right", {"start": v(152.4, -50.8) * mm, "end": v(152.4, -25.4) * mm});
            skLineSegment(sketch, "E94.top", {"start": v(-127, -25.4) * mm, "end": v(-101.6, -25.4) * mm});
            skLineSegment(sketch, "E94.left", {"start": v(-127, 0) * mm, "end": v(-127, -25.4) * mm});
            skLineSegment(sketch, "E94.right", {"start": v(-101.6, 0) * mm, "end": v(-101.6, -25.4) * mm});
            skLineSegment(sketch, "E95.bottom", {"start": v(-101.6, -25.4) * mm, "end": v(-76.2, -25.4) * mm});
            skLineSegment(sketch, "E95.left", {"start": v(-101.6, -25.4) * mm, "end": v(-101.6, 0) * mm});
            skLineSegment(sketch, "E95.right", {"start": v(-76.2, -25.4) * mm, "end": v(-76.2, 0) * mm});
            skLineSegment(sketch, "E96.bottom", {"start": v(-76.2, -25.4) * mm, "end": v(-50.8, -25.4) * mm});
            skLineSegment(sketch, "E96.right", {"start": v(-50.8, -25.4) * mm, "end": v(-50.8, 0) * mm});
            skLineSegment(sketch, "E97.bottom", {"start": v(-50.8, -25.4) * mm, "end": v(-25.4, -25.4) * mm});
            skLineSegment(sketch, "E97.right", {"start": v(-25.4, -25.4) * mm, "end": v(-25.4, 0) * mm});
            skLineSegment(sketch, "E98.bottom", {"start": v(-25.4, -25.4) * mm, "end": v(0, -25.4) * mm});
            skLineSegment(sketch, "E98.right", {"start": v(0, -25.4) * mm, "end": v(0, 0) * mm});
            skLineSegment(sketch, "E99.bottom", {"start": v(0, -25.4) * mm, "end": v(25.4, -25.4) * mm});
            skLineSegment(sketch, "E99.right", {"start": v(25.4, -25.4) * mm, "end": v(25.4, 0) * mm});
            skLineSegment(sketch, "E100.bottom", {"start": v(25.4, -25.4) * mm, "end": v(50.8, -25.4) * mm});
            skLineSegment(sketch, "E100.right", {"start": v(50.8, -25.4) * mm, "end": v(50.8, 0) * mm});
            skLineSegment(sketch, "E101.bottom", {"start": v(50.8, -25.4) * mm, "end": v(76.2, -25.4) * mm});
            skLineSegment(sketch, "E101.right", {"start": v(76.2, -25.4) * mm, "end": v(76.2, 0) * mm});
            skLineSegment(sketch, "E102.bottom", {"start": v(76.2, -25.4) * mm, "end": v(101.6, -25.4) * mm});
            skLineSegment(sketch, "E102.right", {"start": v(101.6, -25.4) * mm, "end": v(101.6, 0) * mm});
            skLineSegment(sketch, "E103.bottom", {"start": v(101.6, -25.4) * mm, "end": v(127, -25.4) * mm});
            skLineSegment(sketch, "E103.right", {"start": v(127, -25.4) * mm, "end": v(127, 0) * mm});
            skSolve(sketch);
        }
        {
            var Q0;
            Q0=makeQuery(id+"F25.imprint","IMPRINT",FACE,{"disambiguationData":[TD([[makeQuery(id+"F25.imprint","IMPRINT",EDGE,{"derivedFrom":sQuery(id+"F25.wireOp",EDGE,"E83.bottom")}),-1.0]])]});
            var Q1;
            Q1=makeQuery(id+"F25.imprint","IMPRINT",FACE,{"disambiguationData":[TD([[makeQuery(id+"F25.imprint","IMPRINT",EDGE,{"derivedFrom":sQuery(id+"F25.wireOp",EDGE,"E95.bottom")}),1.0]])]});
            var Q2;
            Q2=makeQuery(id+"F25.imprint","IMPRINT",FACE,{"disambiguationData":[TD([[makeQuery(id+"F25.imprint","IMPRINT",EDGE,{"derivedFrom":sQuery(id+"F25.wireOp",EDGE,"E85.top")}),-1.0]])]});
            var Q3;
            Q3=makeQuery(id+"F25.imprint","IMPRINT",FACE,{"disambiguationData":[TD([[makeQuery(id+"F25.imprint","IMPRINT",EDGE,{"derivedFrom":sQuery(id+"F25.wireOp",EDGE,"E97.bottom")}),1.0]])]});
            var Q4;
            Q4=makeQuery(id+"F25.imprint","IMPRINT",FACE,{"disambiguationData":[TD([[makeQuery(id+"F25.imprint","IMPRINT",EDGE,{"derivedFrom":sQuery(id+"F25.wireOp",EDGE,"E87.top")}),-1.0]])]});
            var Q5;
            Q5=makeQuery(id+"F25.imprint","IMPRINT",FACE,{"disambiguationData":[TD([[makeQuery(id+"F25.imprint","IMPRINT",EDGE,{"derivedFrom":sQuery(id+"F25.wireOp",EDGE,"E99.bottom")}),1.0]])]});
            var Q6;
            Q6=makeQuery(id+"F25.imprint","IMPRINT",FACE,{"disambiguationData":[TD([[makeQuery(id+"F25.imprint","IMPRINT",EDGE,{"derivedFrom":sQuery(id+"F25.wireOp",EDGE,"E89.top")}),-1.0]])]});
            var Q7;
            Q7=makeQuery(id+"F25.imprint","IMPRINT",FACE,{"disambiguationData":[TD([[makeQuery(id+"F25.imprint","IMPRINT",EDGE,{"derivedFrom":sQuery(id+"F25.wireOp",EDGE,"E101.bottom")}),1.0]])]});
            var Q8;
            Q8=makeQuery(id+"F25.imprint","IMPRINT",FACE,{"disambiguationData":[TD([[makeQuery(id+"F25.imprint","IMPRINT",EDGE,{"derivedFrom":sQuery(id+"F25.wireOp",EDGE,"E91.top")}),-1.0]])]});
            var Q9;
            Q9=makeQuery(id+"F25.imprint","IMPRINT",FACE,{"disambiguationData":[TD([[makeQuery(id+"F25.imprint","IMPRINT",EDGE,{"derivedFrom":sQuery(id+"F25.wireOp",EDGE,"E103.bottom")}),1.0]])]});
            extrude(context, id + "F26", {"entities" : qUnion([Q0, Q1, Q2, Q3, Q4, Q5, Q6, Q7, Q8, Q9]), "operationType" : NewBodyOperationType.ADD, "depth" : 25.4 * mm, "hasDraft" : true, "draftAngle" : 35 * degree, "draftPullDirection" : true});
        }
        {
            var Q0;
            Q0=makeQuery(id+"F25.imprint","IMPRINT",FACE,{"disambiguationData":[TD([[makeQuery(id+"F25.imprint","IMPRINT",EDGE,{"derivedFrom":sQuery(id+"F25.wireOp",EDGE,"E83.top")}),-1.0]])]});
            var Q1;
            Q1=makeQuery(id+"F25.imprint","IMPRINT",FACE,{"disambiguationData":[TD([[makeQuery(id+"F25.imprint","IMPRINT",EDGE,{"derivedFrom":sQuery(id+"F25.wireOp",EDGE,"E84.top")}),-1.0]])]});
            var Q2;
            Q2=makeQuery(id+"F25.imprint","IMPRINT",FACE,{"disambiguationData":[TD([[makeQuery(id+"F25.imprint","IMPRINT",EDGE,{"derivedFrom":sQuery(id+"F25.wireOp",EDGE,"E96.bottom")}),1.0]])]});
            var Q3;
            Q3=makeQuery(id+"F25.imprint","IMPRINT",FACE,{"disambiguationData":[TD([[makeQuery(id+"F25.imprint","IMPRINT",EDGE,{"derivedFrom":sQuery(id+"F25.wireOp",EDGE,"E86.top")}),-1.0]])]});
            var Q4;
            Q4=makeQuery(id+"F25.imprint","IMPRINT",FACE,{"disambiguationData":[TD([[makeQuery(id+"F25.imprint","IMPRINT",EDGE,{"derivedFrom":sQuery(id+"F25.wireOp",EDGE,"E98.bottom")}),1.0]])]});
            var Q5;
            Q5=makeQuery(id+"F25.imprint","IMPRINT",FACE,{"disambiguationData":[TD([[makeQuery(id+"F25.imprint","IMPRINT",EDGE,{"derivedFrom":sQuery(id+"F25.wireOp",EDGE,"E88.top")}),-1.0]])]});
            var Q6;
            Q6=makeQuery(id+"F25.imprint","IMPRINT",FACE,{"disambiguationData":[TD([[makeQuery(id+"F25.imprint","IMPRINT",EDGE,{"derivedFrom":sQuery(id+"F25.wireOp",EDGE,"E100.bottom")}),1.0]])]});
            var Q7;
            Q7=makeQuery(id+"F25.imprint","IMPRINT",FACE,{"disambiguationData":[TD([[makeQuery(id+"F25.imprint","IMPRINT",EDGE,{"derivedFrom":sQuery(id+"F25.wireOp",EDGE,"E90.top")}),-1.0]])]});
            var Q8;
            Q8=makeQuery(id+"F25.imprint","IMPRINT",FACE,{"disambiguationData":[TD([[makeQuery(id+"F25.imprint","IMPRINT",EDGE,{"derivedFrom":sQuery(id+"F25.wireOp",EDGE,"E92.top")}),-1.0]])]});
            var Q9;
            Q9=makeQuery(id+"F25.imprint","IMPRINT",FACE,{"disambiguationData":[TD([[makeQuery(id+"F25.imprint","IMPRINT",EDGE,{"derivedFrom":sQuery(id+"F25.wireOp",EDGE,"E102.bottom")}),1.0]])]});
            extrude(context, id + "F27", {"entities" : qUnion([Q0, Q1, Q2, Q3, Q4, Q5, Q6, Q7, Q8, Q9]), "operationType" : NewBodyOperationType.ADD, "depth" : 25.4 * mm, "hasDraft" : true, "draftAngle" : 35 * degree, "draftPullDirection" : true});
        }
        {
            var Q0;
            Q0=makeQuery(id+"F24.boolean.opBoolean","MERGE",EDGE,{"derivedFrom":[makeQuery(id+"F10.opExtrude","CAP_EDGE",EDGE,{"disambiguationData":[OSD([sQuery(id+"F9.wireOp",EDGE,"E9.right")])],"isStart":false}),makeQuery(id+"F24.opExtrude","CAP_EDGE",EDGE,{"disambiguationData":[OSD([sQuery(id+"F23.wireOp",EDGE,"E82.right")])],"isStart":false})]});
            var Q1;
            Q1=makeQuery(id+"F24.opExtrude","CAP_EDGE",EDGE,{"disambiguationData":[OSD([sQuery(id+"F23.wireOp",EDGE,"E82.top")])],"isStart":false});
            var Q2;
            Q2=makeQuery(id+"F24.boolean.opBoolean","MERGE",EDGE,{"derivedFrom":[makeQuery(id+"F10.opExtrude","CAP_EDGE",EDGE,{"disambiguationData":[OSD([sQuery(id+"F9.wireOp",EDGE,"E9.left")])],"isStart":false}),makeQuery(id+"F24.opExtrude","CAP_EDGE",EDGE,{"disambiguationData":[OSD([sQuery(id+"F23.wireOp",EDGE,"E82.left")])],"isStart":false})]});
            chamfer(context, id + "F28", {"entities" : qUnion([Q0, Q1, Q2]), "width" : 25.4 * mm, "tangentPropagation" : true});
        }
        {
            var Q0;
            Q0=makeQuery(id+"F24.boolean.opBoolean","MERGE",FACE,{"derivedFrom":[makeQuery(id+"F19.boolean.opBoolean","MERGE",FACE,{"derivedFrom":[makeQuery(id+"F10.boolean.opBoolean","MERGE",FACE,{"derivedFrom":[makeQuery(id+"F5.boolean.opBoolean","MERGE",FACE,{"derivedFrom":[makeQuery(id+"F3.boolean.opBoolean","MERGE",FACE,{"derivedFrom":[makeQuery(id+"F1.opExtrude","SWEPT_FACE",FACE,{"disambiguationData":[OSD([sQuery(id+"F0.wireOp",EDGE,"E0.left")])]}),makeQuery(id+"F3.opExtrude","SWEPT_FACE",FACE,{"disambiguationData":[OSD([sQuery(id+"F2.wireOp",EDGE,"E1.left")])]})]}),makeQuery(id+"F5.opExtrude","SWEPT_FACE",FACE,{"disambiguationData":[OSD([sQuery(id+"F4.wireOp",EDGE,"E5.right")])]})]}),makeQuery(id+"F10.opExtrude","SWEPT_FACE",FACE,{"disambiguationData":[OSD([sQuery(id+"F9.wireOp",EDGE,"E9.left")])]})]}),makeQuery(id+"F19.opExtrude","SWEPT_FACE",FACE,{"disambiguationData":[OSD([sQuery(id+"F18.wireOp",EDGE,"E75.left"),sQuery(id+"F18.wireOp",EDGE,"E77.left")])]})]}),makeQuery(id+"F24.opExtrude","SWEPT_FACE",FACE,{"disambiguationData":[OSD([sQuery(id+"F23.wireOp",EDGE,"E82.left")])]})]});
            var sketch = newSketch(context, id + "F29", { "sketchPlane" : qUnion([Q0])});
            skCircle(sketch, "E104", {"center": v(-59.98, -25.4) * mm, "radius": 19.05 * mm});
            skLineSegment(sketch, "E105", {"start": v(-59.98, -25.4) * mm, "end": v(67.02, -25.4) * mm, "construction": true});
            skCircle(sketch, "E106", {"center": v(67.02, -25.4) * mm, "radius": 19.05 * mm});
            skSolve(sketch);
        }
        {
            var Q0;
            Q0=sQuery(id+"F29.wireOp",VERTEX,"E105.start");
            var Q1;
            Q1=sQuery(id+"F29.wireOp",VERTEX,"E106.center");
            var Q2;
            Q2=makeQuery(id+"F1.opExtrude","SWEPT_BODY",BODY,{"disambiguationData":[OSD([sQuery(id+"F0.wireOp",EDGE,"E0.bottom"),sQuery(id+"F0.wireOp",EDGE,"E0.top"),sQuery(id+"F0.wireOp",EDGE,"E0.left"),sQuery(id+"F0.wireOp",EDGE,"E0.right")])]});
            hole(context, id + "F30", {"style" : HoleStyle.SIMPLE, "endStyle" : HoleEndStyle.THROUGH, "holeDiameter" : 38.1 * mm, "isTappedThrough" : true, "tappedDepth" : 12.7 * mm, "tapClearance" : 3, "locations" : qUnion([Q0, Q1]), "scope" : qUnion([Q2])});
        }
        {
            var Q0;
            Q0=makeQuery(id+"F19.opExtrude","CAP_EDGE",EDGE,{"disambiguationData":[OSD([sQuery(id+"F18.wireOp",EDGE,"E75.top")])],"isStart":false});
            var Q1;
            Q1=makeQuery(id+"F19.opExtrude","CAP_EDGE",EDGE,{"disambiguationData":[OSD([sQuery(id+"F18.wireOp",EDGE,"E78.top")])],"isStart":false});
            chamfer(context, id + "F31", {"entities" : qUnion([Q0, Q1]), "width" : 50.8 * mm, "tangentPropagation" : true});
        }
    });
